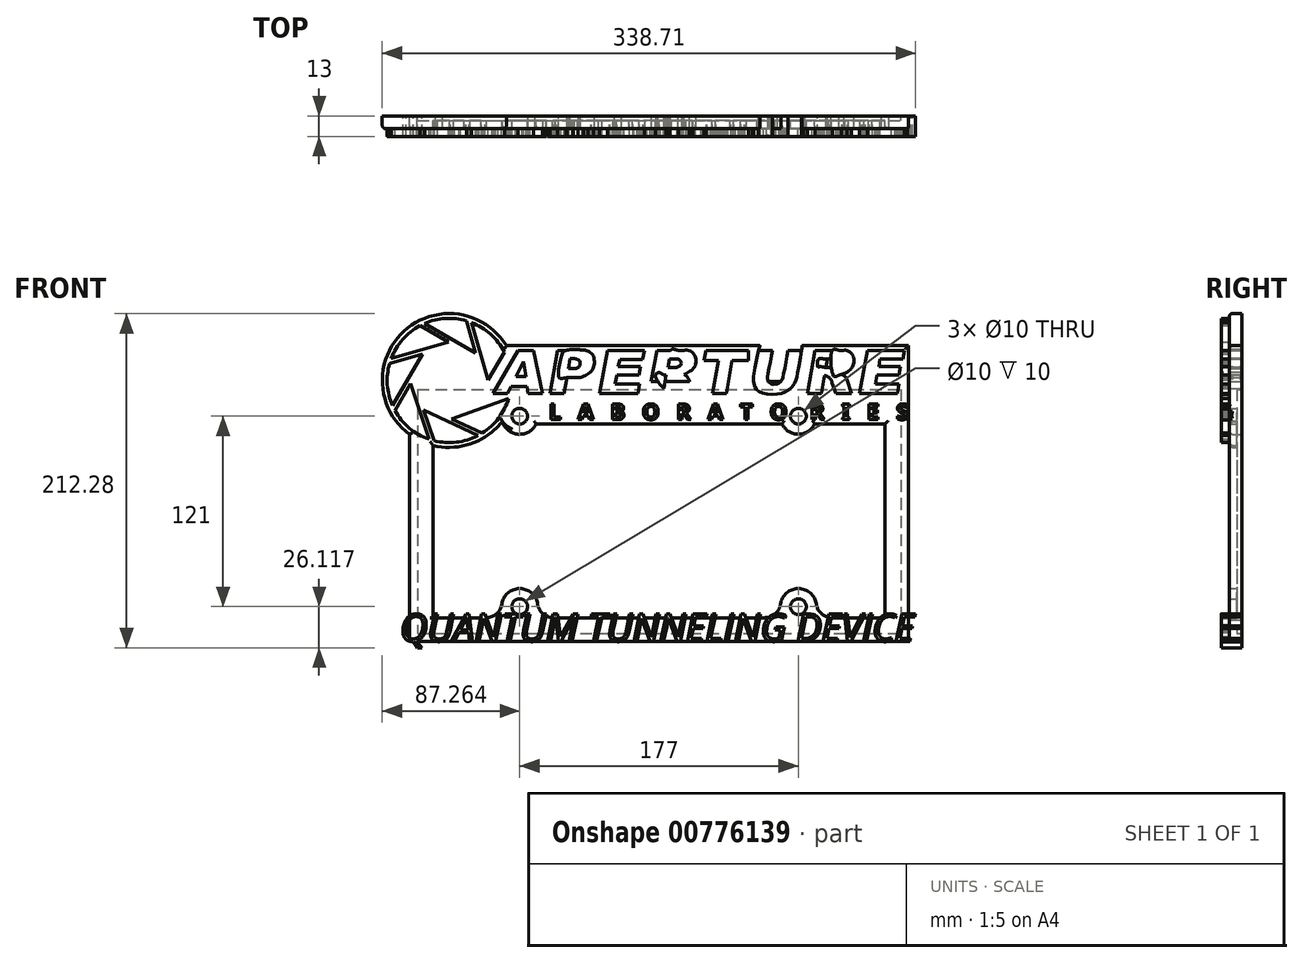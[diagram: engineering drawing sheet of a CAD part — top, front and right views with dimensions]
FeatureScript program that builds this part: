
annotation { "Feature Type Name" : "Feature", "Feature Type Description" : "" }
export const myFeature = defineFeature(function(context is Context, id is Id, definition is map)
    precondition{}
    {
        {
            var Q0;
            Q0=qCreatedBy(makeId("Front.planeOp"),FACE);
            var sketch = newSketch(context, id + "F0", { "sketchPlane" : qUnion([Q0])});
            skLineSegment(sketch, "E0.bottom", {"start": v(-247.83, 125.5) * mm, "end": v(59.17, 125.5) * mm});
            skLineSegment(sketch, "E0.top", {"start": v(-247.83, -29.5) * mm, "end": v(59.17, -29.5) * mm});
            skLineSegment(sketch, "E0.left", {"start": v(-247.83, 125.5) * mm, "end": v(-247.83, -29.5) * mm});
            skLineSegment(sketch, "E0.right", {"start": v(59.17, 125.5) * mm, "end": v(59.17, -29.5) * mm});
            skCircle(sketch, "E1", {"center": v(-182.83, 108.5) * mm, "radius": 5 * mm});
            skCircle(sketch, "E2", {"center": v(-5.83, 108.5) * mm, "radius": 5 * mm});
            skCircle(sketch, "E3", {"center": v(-182.83, -12.5) * mm, "radius": 5 * mm});
            skCircle(sketch, "E4", {"center": v(-5.83, -12.5) * mm, "radius": 5 * mm});
            skLineSegment(sketch, "E5.bottom", {"start": v(-252.83, 130.5) * mm, "end": v(64.17, 130.5) * mm});
            skLineSegment(sketch, "E5.top", {"start": v(-252.83, -34.5) * mm, "end": v(64.17, -34.5) * mm});
            skLineSegment(sketch, "E5.left", {"start": v(-252.83, 130.5) * mm, "end": v(-252.83, -34.5) * mm});
            skLineSegment(sketch, "E5.right", {"start": v(64.17, 130.5) * mm, "end": v(64.17, -34.5) * mm});
            skLineSegment(sketch, "E6.bottom", {"start": v(49.17, 115.5) * mm, "end": v(15.46, 115.5) * mm});
            skLineSegment(sketch, "E6.top", {"start": v(49.17, -19.5) * mm, "end": v(15.46, -19.5) * mm});
            skLineSegment(sketch, "E6.left", {"start": v(49.17, 115.5) * mm, "end": v(49.17, -19.5) * mm});
            skLineSegment(sketch, "E6.right", {"start": v(-237.83, 115.5) * mm, "end": v(-237.83, -19.5) * mm});
            skArc(sketch, "E7", {"start": v(-17.21, 106.9) * mm, "mid": v(-5.83, 97) * mm, "end": v(5.56, 106.9) * mm});
            skArc(sketch, "E8", {"start": v(-194.21, 106.9) * mm, "mid": v(-182.83, 97) * mm, "end": v(-171.44, 106.9) * mm});
            skArc(sketch, "E9", {"start": v(-171.44, -10.89) * mm, "mid": v(-182.83, -1) * mm, "end": v(-194.21, -10.89) * mm});
            skLineSegment(sketch, "E10.trimOffspring", {"start": v(-204.12, -19.5) * mm, "end": v(-237.83, -19.5) * mm});
            skLineSegment(sketch, "E11.trimOffspring", {"start": v(-204.12, 115.5) * mm, "end": v(-237.83, 115.5) * mm});
            skLineSegment(sketch, "E12.trimOffspring", {"start": v(-27.12, 115.5) * mm, "end": v(-161.54, 115.5) * mm});
            skArc(sketch, "E13", {"start": v(5.56, -10.89) * mm, "mid": v(-5.83, -1) * mm, "end": v(-17.21, -10.89) * mm});
            skLineSegment(sketch, "E14.trimOffspring", {"start": v(-27.12, -19.5) * mm, "end": v(-161.54, -19.5) * mm});
            skPoint(sketch, "E15.visualSharp", {"position": v(-173.7, -19.5) * mm});
            skArc(sketch, "E15.filletArc", {"start": v(-171.44, -10.89) * mm, "mid": v(-168.1, -17.04) * mm, "end": v(-161.54, -19.5) * mm});
            skPoint(sketch, "E16.visualSharp", {"position": v(-191.95, -19.5) * mm});
            skArc(sketch, "E16.filletArc", {"start": v(-204.12, -19.5) * mm, "mid": v(-197.56, -17.04) * mm, "end": v(-194.21, -10.89) * mm});
            skPoint(sketch, "E17.visualSharp", {"position": v(-14.95, -19.5) * mm});
            skArc(sketch, "E17.filletArc", {"start": v(-27.12, -19.5) * mm, "mid": v(-20.56, -17.04) * mm, "end": v(-17.21, -10.89) * mm});
            skPoint(sketch, "E18.visualSharp", {"position": v(3.3, -19.5) * mm});
            skArc(sketch, "E18.filletArc", {"start": v(5.56, -10.89) * mm, "mid": v(8.9, -17.04) * mm, "end": v(15.46, -19.5) * mm});
            skPoint(sketch, "E19.visualSharp", {"position": v(3.3, 115.5) * mm});
            skArc(sketch, "E19.filletArc", {"start": v(15.46, 115.5) * mm, "mid": v(8.9, 113.05) * mm, "end": v(5.56, 106.9) * mm});
            skPoint(sketch, "E20.visualSharp", {"position": v(-14.95, 115.5) * mm});
            skArc(sketch, "E20.filletArc", {"start": v(-17.21, 106.9) * mm, "mid": v(-20.56, 113.05) * mm, "end": v(-27.12, 115.5) * mm});
            skPoint(sketch, "E21.visualSharp", {"position": v(-173.7, 115.5) * mm});
            skArc(sketch, "E21.filletArc", {"start": v(-161.54, 115.5) * mm, "mid": v(-168.1, 113.05) * mm, "end": v(-171.44, 106.9) * mm});
            skPoint(sketch, "E22.visualSharp", {"position": v(-191.95, 115.5) * mm});
            skArc(sketch, "E22.filletArc", {"start": v(-194.21, 106.9) * mm, "mid": v(-197.56, 113.05) * mm, "end": v(-204.12, 115.5) * mm});
            skSolve(sketch);
        }
        {
            var Q0;
            Q0=qCreatedBy(makeId("Front.planeOp"),FACE);
            var sketch = newSketch(context, id + "F1", { "sketchPlane" : qUnion([Q0])});
            skArc(sketch, "E23", {"start": v(-237.3, 92.95) * mm, "mid": v(-223.07, 92) * mm, "end": v(-209.42, 96.17) * mm});
            skPoint(sketch, "E23.first.point", {"position": v(-258.83, 155.25) * mm});
            skPoint(sketch, "E23.second.point", {"position": v(-223.83, 91.92) * mm});
            skPoint(sketch, "E23.third.point", {"position": v(-267, 132.67) * mm});
            skLineSegment(sketch, "E24", {"start": v(-246.07, 166.01) * mm, "end": v(-228.04, 155.5) * mm});
            skLineSegment(sketch, "E25", {"start": v(-228.04, 155.5) * mm, "end": v(-264.5, 145.07) * mm});
            skLineSegment(sketch, "E26", {"start": v(-243.18, 167.4) * mm, "end": v(-210.8, 148.54) * mm});
            skLineSegment(sketch, "E27", {"start": v(-210.8, 148.54) * mm, "end": v(-216.68, 169.07) * mm});
            skLineSegment(sketch, "E28", {"start": v(-213.44, 167.98) * mm, "end": v(-203, 131.5) * mm});
            skLineSegment(sketch, "E29", {"start": v(-203, 131.5) * mm, "end": v(-192.6, 149.36) * mm});
            skLineSegment(sketch, "E30", {"start": v(-265.5, 142.08) * mm, "end": v(-244.59, 148.07) * mm});
            skLineSegment(sketch, "E31", {"start": v(-244.59, 148.07) * mm, "end": v(-263.68, 115.27) * mm});
            skLineSegment(sketch, "E32", {"start": v(-262.1, 112.08) * mm, "end": v(-252.17, 129.12) * mm});
            skLineSegment(sketch, "E33", {"start": v(-252.17, 129.12) * mm, "end": v(-240.5, 93.9) * mm});
            skLineSegment(sketch, "E34", {"start": v(-237.3, 92.95) * mm, "end": v(-243.8, 112.5) * mm});
            skLineSegment(sketch, "E35", {"start": v(-243.8, 112.5) * mm, "end": v(-209.42, 96.17) * mm});
            skLineSegment(sketch, "E36", {"start": v(-206.72, 97.71) * mm, "end": v(-226, 106.88) * mm});
            skLineSegment(sketch, "E37", {"start": v(-226, 106.88) * mm, "end": v(-189.8, 119.9) * mm});
            skArc(sketch, "E38.trimOffspring", {"start": v(-206.72, 97.71) * mm, "mid": v(-196.24, 107.26) * mm, "end": v(-189.8, 119.9) * mm});
            skArc(sketch, "E39.trimOffspring", {"start": v(-262.1, 112.08) * mm, "mid": v(-252.98, 101) * mm, "end": v(-240.5, 93.9) * mm});
            skArc(sketch, "E40.trimOffspring", {"start": v(-265.5, 142.08) * mm, "mid": v(-266.94, 128.52) * mm, "end": v(-263.68, 115.27) * mm});
            skArc(sketch, "E41.trimOffspring", {"start": v(-246.07, 166.01) * mm, "mid": v(-257.2, 157.22) * mm, "end": v(-264.5, 145.07) * mm});
            skArc(sketch, "E42.trimOffspring", {"start": v(-216.68, 169.07) * mm, "mid": v(-230.08, 170.53) * mm, "end": v(-243.18, 167.4) * mm});
            skArc(sketch, "E43.trimOffspring", {"start": v(-192.6, 149.36) * mm, "mid": v(-201.32, 160.58) * mm, "end": v(-213.44, 167.98) * mm});
            skArc(sketch, "E44", {"start": v(-191.32, 153.32) * mm, "mid": v(-269.71, 136.84) * mm, "end": v(-198.47, 100.23) * mm});
            skLineSegment(sketch, "E45", {"start": v(-191.32, 153.32) * mm, "end": v(64.17, 153.32) * mm});
            skLineSegment(sketch, "E46", {"start": v(64.17, 153.32) * mm, "end": v(64.17, 128.47) * mm});
            skLineSegment(sketch, "E47", {"start": v(-199.68, 123) * mm, "end": v(-183.75, 150.32) * mm});
            skLineSegment(sketch, "E48", {"start": v(-183.75, 150.32) * mm, "end": v(-174.2, 150.32) * mm});
            skLineSegment(sketch, "E49", {"start": v(-174.2, 150.32) * mm, "end": v(-168.23, 123) * mm});
            skLineSegment(sketch, "E50", {"start": v(-168.23, 123) * mm, "end": v(-177.57, 123) * mm});
            skLineSegment(sketch, "E51", {"start": v(-177.57, 123) * mm, "end": v(-178.26, 127.46) * mm});
            skLineSegment(sketch, "E52", {"start": v(-178.26, 127.46) * mm, "end": v(-188.28, 127.46) * mm});
            skLineSegment(sketch, "E53", {"start": v(-188.28, 127.46) * mm, "end": v(-190.41, 123) * mm});
            skLineSegment(sketch, "E54", {"start": v(-190.41, 123) * mm, "end": v(-199.68, 123) * mm});
            skLineSegment(sketch, "E55", {"start": v(-185.06, 133.84) * mm, "end": v(-180.46, 143.25) * mm});
            skLineSegment(sketch, "E56", {"start": v(-180.46, 143.25) * mm, "end": v(-178.88, 133.64) * mm});
            skLineSegment(sketch, "E57", {"start": v(-178.88, 133.64) * mm, "end": v(-185.06, 133.84) * mm});
            skLineSegment(sketch, "E58", {"start": v(-163.56, 123) * mm, "end": v(-158.67, 150.32) * mm});
            skLineSegment(sketch, "E59", {"start": v(-158.67, 150.32) * mm, "end": v(-140.86, 150.32) * mm});
            skLineSegment(sketch, "E60", {"start": v(-163.56, 123) * mm, "end": v(-154.65, 123) * mm});
            skLineSegment(sketch, "E61", {"start": v(-154.65, 123) * mm, "end": v(-152.8, 133.06) * mm});
            skLineSegment(sketch, "E62", {"start": v(-152.8, 133.06) * mm, "end": v(-145.58, 133.06) * mm});
            skLineSegment(sketch, "E63", {"start": v(-150.74, 145) * mm, "end": v(-151.94, 138.81) * mm});
            skPoint(sketch, "E64.12.internal.snap0", {"position": v(-151.34, 141.9) * mm});
            skFitSpline(sketch, "E64", {"points": [v(-150.74, 145) * mm, v(-147.48, 145) * mm, v(-145.9, 144.52) * mm, v(-144.71, 143.37) * mm, v(-144.5, 142.29) * mm, v(-144.66, 140.5) * mm, v(-145.9, 139.4) * mm, v(-147.8, 138.76) * mm, v(-151.94, 138.81) * mm, v(-153.46, 138.81) * mm, v(-155.03, 138.81) * mm, v(-155.2, 140.17) * mm, v(-154.65, 141.9) * mm, v(-153.9, 145) * mm, v(-152.75, 145) * mm, v(-150.74, 145) * mm]});
            skFitSpline(sketch, "E65", {"points": [v(-140.86, 150.32) * mm, v(-138.78, 149.57) * mm, v(-136.84, 148.03) * mm, v(-135.81, 146.08) * mm, v(-135.45, 143.16) * mm, v(-135.7, 140.7) * mm, v(-136.84, 137.77) * mm, v(-138.02, 136.39) * mm, v(-140.02, 134.85) * mm, v(-142.68, 133.67) * mm, v(-145.58, 133.06) * mm, v(-152.8, 133.06) * mm, v(-157.81, 133.06) * mm, v(-156.38, 146.6) * mm, v(-153.56, 150.32) * mm, v(-140.86, 150.32) * mm]});
            skLineSegment(sketch, "E66", {"start": v(-127.1, 150.38) * mm, "end": v(-103.53, 150.38) * mm});
            skLineSegment(sketch, "E67", {"start": v(-103.53, 150.38) * mm, "end": v(-104.72, 144.46) * mm});
            skLineSegment(sketch, "E68", {"start": v(-104.72, 144.46) * mm, "end": v(-119.26, 144.46) * mm});
            skLineSegment(sketch, "E69", {"start": v(-119.26, 144.46) * mm, "end": v(-120.24, 140.2) * mm});
            skLineSegment(sketch, "E70", {"start": v(-120.24, 140.2) * mm, "end": v(-106.23, 140.2) * mm});
            skLineSegment(sketch, "E71", {"start": v(-106.23, 140.2) * mm, "end": v(-107.21, 134.6) * mm});
            skLineSegment(sketch, "E72", {"start": v(-107.21, 134.6) * mm, "end": v(-121.12, 134.6) * mm});
            skLineSegment(sketch, "E73", {"start": v(-121.12, 134.6) * mm, "end": v(-122.21, 129.04) * mm});
            skLineSegment(sketch, "E74", {"start": v(-122.21, 129.04) * mm, "end": v(-106.85, 129.04) * mm});
            skLineSegment(sketch, "E75", {"start": v(-106.85, 129.04) * mm, "end": v(-107.84, 122.92) * mm});
            skLineSegment(sketch, "E76", {"start": v(-107.84, 122.92) * mm, "end": v(-132.23, 122.92) * mm});
            skLineSegment(sketch, "E77", {"start": v(-132.23, 122.92) * mm, "end": v(-127.1, 150.38) * mm});
            skLineSegment(sketch, "E78", {"start": v(-64.64, 150.38) * mm, "end": v(-37.58, 150.38) * mm});
            skLineSegment(sketch, "E79", {"start": v(-37.58, 150.38) * mm, "end": v(-37.58, 143.85) * mm});
            skLineSegment(sketch, "E80", {"start": v(-37.58, 143.85) * mm, "end": v(-47.88, 143.85) * mm});
            skLineSegment(sketch, "E81", {"start": v(-47.88, 143.85) * mm, "end": v(-51.56, 122.92) * mm});
            skLineSegment(sketch, "E82", {"start": v(-51.56, 122.92) * mm, "end": v(-60.33, 122.92) * mm});
            skLineSegment(sketch, "E83", {"start": v(-60.33, 122.92) * mm, "end": v(-56.65, 143.85) * mm});
            skLineSegment(sketch, "E84", {"start": v(-56.65, 143.85) * mm, "end": v(-65.71, 143.85) * mm});
            skLineSegment(sketch, "E85", {"start": v(-65.71, 143.85) * mm, "end": v(-64.64, 150.38) * mm});
            skLineSegment(sketch, "E86", {"start": v(38.19, 150.38) * mm, "end": v(61.68, 150.38) * mm});
            skLineSegment(sketch, "E87", {"start": v(61.68, 150.38) * mm, "end": v(60.69, 144.74) * mm});
            skLineSegment(sketch, "E88", {"start": v(60.69, 144.74) * mm, "end": v(46.1, 144.74) * mm});
            skLineSegment(sketch, "E89", {"start": v(46.1, 144.74) * mm, "end": v(45.31, 140.2) * mm});
            skLineSegment(sketch, "E90", {"start": v(45.31, 140.2) * mm, "end": v(59.09, 140.2) * mm});
            skLineSegment(sketch, "E91", {"start": v(59.09, 140.2) * mm, "end": v(58.1, 134.6) * mm});
            skLineSegment(sketch, "E92", {"start": v(58.1, 134.6) * mm, "end": v(44.13, 134.6) * mm});
            skLineSegment(sketch, "E93", {"start": v(44.13, 134.6) * mm, "end": v(43.15, 129.04) * mm});
            skLineSegment(sketch, "E94", {"start": v(43.15, 129.04) * mm, "end": v(58.1, 129.04) * mm});
            skLineSegment(sketch, "E95", {"start": v(58.1, 129.04) * mm, "end": v(57.02, 122.92) * mm});
            skLineSegment(sketch, "E96", {"start": v(57.02, 122.92) * mm, "end": v(33, 122.92) * mm});
            skLineSegment(sketch, "E97", {"start": v(33, 122.92) * mm, "end": v(38.19, 150.38) * mm});
            skLineSegment(sketch, "E98", {"start": v(-89.8, 134.6) * mm, "end": v(-91.85, 122.92) * mm});
            skLineSegment(sketch, "E99", {"start": v(-91.85, 122.92) * mm, "end": v(-100.78, 122.92) * mm});
            skLineSegment(sketch, "E100", {"start": v(-100.78, 122.92) * mm, "end": v(-95.52, 150.38) * mm});
            skLineSegment(sketch, "E101", {"start": v(-95.52, 150.38) * mm, "end": v(-78.58, 150.38) * mm});
            skLineSegment(sketch, "E102", {"start": v(-72.38, 122.92) * mm, "end": v(-82.38, 122.92) * mm});
            skLineSegment(sketch, "E103", {"start": v(-87.64, 144.93) * mm, "end": v(-88.6, 139.45) * mm});
            skLineSegment(sketch, "E104", {"start": v(-31.18, 150.38) * mm, "end": v(-22.4, 150.38) * mm});
            skLineSegment(sketch, "E105", {"start": v(-12.5, 150.38) * mm, "end": v(-3.78, 150.38) * mm});
            skLineSegment(sketch, "E106", {"start": v(27.9, 122.92) * mm, "end": v(18.18, 122.92) * mm});
            skLineSegment(sketch, "E107", {"start": v(10.75, 134.6) * mm, "end": v(8.7, 122.92) * mm});
            skLineSegment(sketch, "E108", {"start": v(8.7, 122.92) * mm, "end": v(0, 122.92) * mm});
            skLineSegment(sketch, "E109", {"start": v(0, 122.92) * mm, "end": v(4.83, 150.38) * mm});
            skLineSegment(sketch, "E110", {"start": v(4.83, 150.38) * mm, "end": v(23.13, 150.38) * mm});
            skLineSegment(sketch, "E111", {"start": v(12.73, 144.93) * mm, "end": v(11.77, 139.45) * mm});
            skFitSpline(sketch, "E112", {"points": [v(-78.58, 150.38) * mm, v(-76.22, 150.38) * mm, v(-73.84, 149.53) * mm, v(-72, 147.8) * mm, v(-71.08, 145.52) * mm, v(-70.92, 142.87) * mm, v(-71.25, 141.09) * mm, v(-72.38, 138.93) * mm, v(-73.79, 137.57) * mm, v(-76.11, 136.11) * mm, v(-78.58, 135.09) * mm, v(-83.9, 134.6) * mm, v(-88.22, 134.6) * mm, v(-87.05, 150.38) * mm, v(-82.38, 150.38) * mm, v(-78.58, 150.38) * mm]});
            skFitSpline(sketch, "E113", {"points": [v(-78.58, 135.09) * mm, v(-76.98, 134.06) * mm, v(-75.63, 132.22) * mm, v(-74.44, 129.25) * mm, v(-72.38, 122.92) * mm, v(-71.52, 120.49) * mm, v(-70.81, 118.6) * mm, v(-81.14, 127.3) * mm, v(-82, 136.82) * mm, v(-80.22, 136) * mm, v(-78.58, 135.09) * mm]});
            skFitSpline(sketch, "E114", {"points": [v(-89.8, 134.6) * mm, v(-87.36, 133.57) * mm, v(-85.47, 131.25) * mm, v(-85.03, 129.2) * mm, v(-83.95, 126.54) * mm, v(-82.38, 122.92) * mm, v(-80.44, 120.7) * mm, v(-80.65, 118.32) * mm, v(-96.55, 133.68) * mm, v(-94.12, 136.17) * mm, v(-91.1, 134.6) * mm, v(-89.8, 134.6) * mm]});
            skFitSpline(sketch, "E115", {"points": [v(-31.18, 150.38) * mm, v(-34.42, 131.99) * mm, v(-34.21, 129.96) * mm, v(-33.72, 127.64) * mm, v(-32.53, 125.61) * mm, v(-30.3, 123.86) * mm, v(-25.88, 122.46) * mm, v(-19.3, 122.53) * mm, v(-14.96, 123.51) * mm, v(-11.31, 125.82) * mm, v(-8.44, 129.11) * mm, v(-6.9, 132.34) * mm, v(-6.27, 135.98) * mm, v(-3.78, 150.38) * mm, v(-3.05, 155.51) * mm, v(-3.05, 158.8) * mm, v(-30.01, 159.37) * mm, v(-30.3, 156.21) * mm, v(-30.5, 152.36) * mm, v(-31.18, 150.38) * mm]});
            skFitSpline(sketch, "E116", {"points": [v(-22.4, 150.38) * mm, v(-25.29, 134.18) * mm, v(-25.29, 132.02) * mm, v(-24.9, 130.65) * mm, v(-23.92, 129.62) * mm, v(-22.4, 128.88) * mm, v(-20.5, 128.83) * mm, v(-18.74, 129.34) * mm, v(-17.2, 130.3) * mm, v(-16.23, 131.79) * mm, v(-15.6, 133.78) * mm, v(-12.5, 150.38) * mm, v(-11.67, 156.07) * mm, v(-11.27, 158.46) * mm, v(-21.07, 158.92) * mm, v(-21.36, 156.47) * mm, v(-21.87, 155.33) * mm, v(-22.4, 150.38) * mm]});
            skFitSpline(sketch, "E117", {"points": [v(12.73, 144.93) * mm, v(16.74, 144.93) * mm, v(18.3, 144.5) * mm, v(19.87, 143.6) * mm, v(20.28, 142.54) * mm, v(20.02, 141.38) * mm, v(18.86, 140.16) * mm, v(16.8, 139.46) * mm, v(13.71, 139.3) * mm, v(11.77, 139.45) * mm, v(7.65, 139.91) * mm, v(6.39, 139.96) * mm, v(7.1, 144.93) * mm, v(9.67, 144.93) * mm, v(12.73, 144.93) * mm]});
            skFitSpline(sketch, "E118", {"points": [v(23.13, 150.38) * mm, v(24.42, 150.38) * mm, v(26.39, 149.56) * mm, v(27.6, 148.6) * mm, v(28.81, 146.93) * mm, v(29.27, 145.67) * mm, v(29.47, 143.6) * mm, v(29.27, 141.63) * mm, v(28.2, 139.3) * mm, v(26.8, 137.74) * mm, v(25.07, 136.53) * mm, v(23.5, 135.72) * mm, v(21.39, 135.06) * mm, v(19.06, 134.15) * mm, v(16.64, 134) * mm, v(15.78, 150.38) * mm, v(19.82, 150.38) * mm, v(23.13, 150.38) * mm]});
            skArc(sketch, "E119", {"start": v(26.39, 149.56) * mm, "mid": v(24.81, 150.17) * mm, "end": v(23.13, 150.38) * mm});
            skArc(sketch, "E120", {"start": v(15.5, 129.45) * mm, "mid": v(14.07, 132.82) * mm, "end": v(10.69, 134.23) * mm});
            skArc(sketch, "E121", {"start": v(24.93, 131.86) * mm, "mid": v(23.55, 133.9) * mm, "end": v(21.39, 135.06) * mm});
            skLineSegment(sketch, "E122", {"start": v(15.5, 129.45) * mm, "end": v(18.18, 122.92) * mm});
            skLineSegment(sketch, "E123", {"start": v(24.93, 131.86) * mm, "end": v(27.9, 122.92) * mm});
            skText(sketch, "E124", { "text": " L   A   B   O   R   A   T   O    R   I   E   S", "fontName": "NotoSans-Bold.ttf"});
            skLineSegment(sketch, "E125", {"start": v(64.17, 103.55) * mm, "end": v(-171.66, 103.55) * mm});
            skLineSegment(sketch, "E126", {"start": v(64.17, 103.55) * mm, "end": v(64.17, 128.47) * mm});
            skFitSpline(sketch, "E127", {"points": [v(-87.64, 144.93) * mm, v(-83.83, 144.93) * mm, v(-81.83, 144.41) * mm, v(-80.56, 143.47) * mm, v(-80.2, 142.57) * mm, v(-80.4, 141.39) * mm, v(-81.1, 140.49) * mm, v(-82.08, 140) * mm, v(-84.12, 139.38) * mm, v(-85.5, 139.3) * mm, v(-88.6, 139.45) * mm, v(-90.9, 139.45) * mm, v(-92.46, 139.45) * mm, v(-91.93, 145.47) * mm, v(-90.58, 144.93) * mm, v(-88.98, 144.93) * mm, v(-87.64, 144.93) * mm]});
            skText(sketch, "E128", { "text": "QUANTUM TUNNELING DEVICE", "fontName": "OpenSans-Italic.ttf"});
            skLineSegment(sketch, "E129", {"start": v(-171.66, 103.55) * mm, "end": v(-177.35, 103.55) * mm});
            skArc(sketch, "E130", {"start": v(-191.23, 102.4) * mm, "mid": v(-184.13, 101.03) * mm, "end": v(-177.35, 103.55) * mm});
            skPoint(sketch, "E131.visualSharp", {"position": v(-193.14, 103.55) * mm});
            skArc(sketch, "E132", {"start": v(-198.47, 100.23) * mm, "mid": v(-196.08, 102.66) * mm, "end": v(-193.94, 105.3) * mm});
            skArc(sketch, "E133", {"start": v(-193.94, 105.3) * mm, "mid": v(-192.7, 103.75) * mm, "end": v(-191.23, 102.4) * mm});
            const initialGuessF1  = {"E124": [-0.16794, 0.10632, 1, 0, 0.01], "E128": [-0.25883, -0.0345, 1, 0, 0.01742]};
            skSetInitialGuess(sketch, initialGuessF1);
            skSolve(sketch);
        }
        {
            var Q0;
            Q0=makeQuery(id+"F1.imprint","IMPRINT",FACE,{"disambiguationData":[TD([[makeQuery(id+"F1.imprint","IMPRINT",EDGE,{"derivedFrom":sQuery(id+"F1.wireOp",EDGE,"E124.sketch_text.stroke-141")}),-1.0]])]});
            var Q1;
            Q1=makeQuery(id+"F1.imprint","IMPRINT",FACE,{"disambiguationData":[TD([[makeQuery(id+"F1.imprint","IMPRINT",EDGE,{"derivedFrom":sQuery(id+"F1.wireOp",EDGE,"E47")}),-1.0]])]});
            var Q2;
            Q2=makeQuery(id+"F0.imprint","IMPRINT",FACE,{"disambiguationData":[TD([[makeQuery(id+"F0.imprint","IMPRINT",EDGE,{"derivedFrom":sQuery(id+"F0.wireOp",EDGE,"E0.bottom")}),1.0]])]});
            var Q3;
            Q3=makeQuery(id+"F0.imprint","IMPRINT",FACE,{"disambiguationData":[TD([[makeQuery(id+"F0.imprint","IMPRINT",EDGE,{"derivedFrom":sQuery(id+"F0.wireOp",EDGE,"E1")}),1.0]])]});
            var Q4;
            Q4=makeQuery(id+"F0.imprint","IMPRINT",FACE,{"disambiguationData":[TD([[makeQuery(id+"F0.imprint","IMPRINT",EDGE,{"derivedFrom":sQuery(id+"F0.wireOp",EDGE,"E2")}),1.0]])]});
            var Q5;
            Q5=makeQuery(id+"F0.imprint","IMPRINT",FACE,{"disambiguationData":[TD([[makeQuery(id+"F0.imprint","IMPRINT",EDGE,{"derivedFrom":sQuery(id+"F0.wireOp",EDGE,"E3")}),1.0]])]});
            var Q6;
            Q6=makeQuery(id+"F0.imprint","IMPRINT",FACE,{"disambiguationData":[TD([[makeQuery(id+"F0.imprint","IMPRINT",EDGE,{"derivedFrom":sQuery(id+"F0.wireOp",EDGE,"E4")}),1.0]])]});
            var Q7;
            Q7=makeQuery(id+"F0.imprint","IMPRINT",FACE,{"disambiguationData":[TD([[makeQuery(id+"F0.imprint","IMPRINT",EDGE,{"derivedFrom":sQuery(id+"F0.wireOp",EDGE,"E0.bottom")}),-1.0]])]});
            var Q8;
            Q8=makeQuery(id+"F1.imprint","IMPRINT",FACE,{"disambiguationData":[TD([[makeQuery(id+"F1.imprint","IMPRINT",EDGE,{"derivedFrom":sQuery(id+"F1.wireOp",EDGE,"E28")}),1.0]])]});
            var Q9;
            Q9=makeQuery(id+"F1.imprint","IMPRINT",FACE,{"disambiguationData":[TD([[makeQuery(id+"F1.imprint","IMPRINT",EDGE,{"derivedFrom":sQuery(id+"F1.wireOp",EDGE,"E124.sketch_text.stroke-51")}),1.0]])]});
            var Q10;
            Q10=makeQuery(id+"F1.imprint","IMPRINT",FACE,{"disambiguationData":[TD([[makeQuery(id+"F1.imprint","IMPRINT",EDGE,{"derivedFrom":sQuery(id+"F1.wireOp",EDGE,"E23")}),1.0]])]});
            var Q11;
            Q11=makeQuery(id+"F1.imprint","IMPRINT",FACE,{"disambiguationData":[TD([[makeQuery(id+"F1.imprint","IMPRINT",EDGE,{"derivedFrom":sQuery(id+"F1.wireOp",EDGE,"E24")}),-1.0]])]});
            var Q12;
            Q12=makeQuery(id+"F1.imprint","IMPRINT",FACE,{"disambiguationData":[TD([[makeQuery(id+"F1.imprint","IMPRINT",EDGE,{"derivedFrom":sQuery(id+"F1.wireOp",EDGE,"E30")}),-1.0]])]});
            var Q13;
            Q13=makeQuery(id+"F1.imprint","IMPRINT",FACE,{"disambiguationData":[TD([[makeQuery(id+"F1.imprint","IMPRINT",EDGE,{"derivedFrom":sQuery(id+"F1.wireOp",EDGE,"E104")}),-1.0]])]});
            var Q14;
            Q14=makeQuery(id+"F1.imprint","IMPRINT",FACE,{"disambiguationData":[TD([[makeQuery(id+"F1.imprint","IMPRINT",EDGE,{"derivedFrom":sQuery(id+"F1.wireOp",EDGE,"E26")}),1.0]])]});
            var Q15;
            Q15=makeQuery(id+"F1.imprint","IMPRINT",FACE,{"disambiguationData":[TD([[makeQuery(id+"F1.imprint","IMPRINT",EDGE,{"derivedFrom":sQuery(id+"F1.wireOp",EDGE,"E32")}),-1.0]])]});
            var Q16;
            Q16=makeQuery(id+"F1.imprint","IMPRINT",FACE,{"disambiguationData":[TD([[makeQuery(id+"F1.imprint","IMPRINT",EDGE,{"derivedFrom":sQuery(id+"F1.wireOp",EDGE,"E36")}),-1.0]])]});
            var Q17;
            Q17=makeQuery(id+"F1.imprint","IMPRINT",FACE,{"disambiguationData":[TD([[makeQuery(id+"F1.imprint","IMPRINT",EDGE,{"derivedFrom":sQuery(id+"F1.wireOp",EDGE,"E66")}),-1.0]])]});
            var Q18;
            Q18=makeQuery(id+"F1.imprint","IMPRINT",FACE,{"disambiguationData":[TD([[makeQuery(id+"F1.imprint","IMPRINT",EDGE,{"derivedFrom":sQuery(id+"F1.wireOp",EDGE,"E78")}),-1.0]])]});
            var Q19;
            Q19=makeQuery(id+"F1.imprint","IMPRINT",FACE,{"disambiguationData":[TD([[makeQuery(id+"F1.imprint","IMPRINT",EDGE,{"derivedFrom":sQuery(id+"F1.wireOp",EDGE,"E86")}),-1.0]])]});
            var Q20;
            Q20=makeQuery(id+"F1.imprint","IMPRINT",FACE,{"disambiguationData":[TD([[makeQuery(id+"F1.imprint","IMPRINT",EDGE,{"derivedFrom":sQuery(id+"F1.wireOp",EDGE,"E98")}),-1.0]])]});
            var Q21;
            Q21=makeQuery(id+"F1.imprint","IMPRINT",FACE,{"disambiguationData":[TD([[makeQuery(id+"F1.imprint","IMPRINT",EDGE,{"derivedFrom":sQuery(id+"F1.wireOp",EDGE,"E106")}),-1.0]])]});
            var Q22;
            Q22=makeQuery(id+"F1.imprint","IMPRINT",FACE,{"disambiguationData":[TD([[makeQuery(id+"F1.imprint","IMPRINT",EDGE,{"derivedFrom":sQuery(id+"F1.wireOp",EDGE,"E58")}),-1.0]])]});
            var Q23;
            Q23=makeQuery(id+"F1.imprint","IMPRINT",FACE,{"disambiguationData":[TD([[makeQuery(id+"F1.imprint","IMPRINT",EDGE,{"derivedFrom":sQuery(id+"F1.wireOp",EDGE,"E124.sketch_text.stroke-104")}),1.0]])]});
            var Q24;
            Q24=makeQuery(id+"F1.imprint","IMPRINT",FACE,{"disambiguationData":[TD([[makeQuery(id+"F1.imprint","IMPRINT",EDGE,{"derivedFrom":sQuery(id+"F1.wireOp",EDGE,"E124.sketch_text.stroke-129")}),-1.0]])]});
            var Q25;
            Q25=makeQuery(id+"F1.imprint","IMPRINT",FACE,{"disambiguationData":[TD([[makeQuery(id+"F1.imprint","IMPRINT",EDGE,{"derivedFrom":sQuery(id+"F1.wireOp",EDGE,"E124.sketch_text.stroke-153")}),-1.0]])]});
            var Q26;
            Q26=makeQuery(id+"F1.imprint","IMPRINT",FACE,{"disambiguationData":[TD([[makeQuery(id+"F1.imprint","IMPRINT",EDGE,{"derivedFrom":sQuery(id+"F1.wireOp",EDGE,"E124.sketch_text.stroke-76")}),-1.0]])]});
            var Q27;
            Q27=makeQuery(id+"F1.imprint","IMPRINT",FACE,{"disambiguationData":[TD([[makeQuery(id+"F1.imprint","IMPRINT",EDGE,{"derivedFrom":sQuery(id+"F1.wireOp",EDGE,"E124.sketch_text.stroke-37")}),1.0]])]});
            var Q28;
            Q28=makeQuery(id+"F1.imprint","IMPRINT",FACE,{"disambiguationData":[TD([[makeQuery(id+"F1.imprint","IMPRINT",EDGE,{"derivedFrom":sQuery(id+"F1.wireOp",EDGE,"E124.sketch_text.stroke-96")}),-1.0]])]});
            var Q29;
            Q29=makeQuery(id+"F1.imprint","IMPRINT",FACE,{"disambiguationData":[TD([[makeQuery(id+"F1.imprint","IMPRINT",EDGE,{"derivedFrom":sQuery(id+"F1.wireOp",EDGE,"E124.sketch_text.stroke-0")}),-1.0]])]});
            var Q30;
            Q30=makeQuery(id+"F1.imprint","IMPRINT",FACE,{"disambiguationData":[TD([[makeQuery(id+"F1.imprint","IMPRINT",EDGE,{"derivedFrom":sQuery(id+"F1.wireOp",EDGE,"E124.sketch_text.stroke-57")}),-1.0]])]});
            var Q31;
            Q31=makeQuery(id+"F1.imprint","IMPRINT",FACE,{"disambiguationData":[TD([[makeQuery(id+"F1.imprint","IMPRINT",EDGE,{"derivedFrom":sQuery(id+"F1.wireOp",EDGE,"E55")}),-1.0]])]});
            var Q32;
            Q32=makeQuery(id+"F1.imprint","IMPRINT",FACE,{"disambiguationData":[TD([[makeQuery(id+"F1.imprint","IMPRINT",EDGE,{"derivedFrom":sQuery(id+"F1.wireOp",EDGE,"E124.sketch_text.stroke-6")}),-1.0]])]});
            var Q33;
            Q33=makeQuery(id+"F1.imprint","IMPRINT",FACE,{"disambiguationData":[TD([[makeQuery(id+"F1.imprint","IMPRINT",EDGE,{"derivedFrom":sQuery(id+"F1.wireOp",EDGE,"E124.sketch_text.stroke-43")}),-1.0]])]});
            var Q34;
            Q34=makeQuery(id+"F1.imprint","IMPRINT",FACE,{"disambiguationData":[TD([[makeQuery(id+"F1.imprint","IMPRINT",EDGE,{"derivedFrom":sQuery(id+"F1.wireOp",EDGE,"E124.sketch_text.stroke-18")}),-1.0]])]});
            var Q35;
            Q35=makeQuery(id+"F1.imprint","IMPRINT",FACE,{"disambiguationData":[TD([[makeQuery(id+"F1.imprint","IMPRINT",EDGE,{"derivedFrom":sQuery(id+"F1.wireOp",EDGE,"E124.sketch_text.stroke-14")}),1.0]])]});
            var Q36;
            Q36=makeQuery(id+"F1.imprint","IMPRINT",FACE,{"disambiguationData":[TD([[makeQuery(id+"F1.imprint","IMPRINT",EDGE,{"derivedFrom":sQuery(id+"F1.wireOp",EDGE,"E124.sketch_text.stroke-88")}),-1.0]])]});
            var Q37;
            Q37=makeQuery(id+"F1.imprint","IMPRINT",FACE,{"disambiguationData":[TD([[makeQuery(id+"F1.imprint","IMPRINT",EDGE,{"derivedFrom":sQuery(id+"F1.wireOp",EDGE,"E124.sketch_text.stroke-57")}),1.0]])]});
            var Q38;
            Q38=makeQuery(id+"F1.imprint","IMPRINT",FACE,{"disambiguationData":[TD([[makeQuery(id+"F1.imprint","IMPRINT",EDGE,{"derivedFrom":sQuery(id+"F1.wireOp",EDGE,"E124.sketch_text.stroke-30")}),1.0]])]});
            var Q39;
            Q39=makeQuery(id+"F1.imprint","IMPRINT",FACE,{"disambiguationData":[TD([[makeQuery(id+"F1.imprint","IMPRINT",EDGE,{"derivedFrom":sQuery(id+"F1.wireOp",EDGE,"E124.sketch_text.stroke-110")}),-1.0]])]});
            var Q40;
            Q40=makeQuery(id+"F1.imprint","IMPRINT",FACE,{"disambiguationData":[TD([[makeQuery(id+"F1.imprint","IMPRINT",EDGE,{"derivedFrom":sQuery(id+"F1.wireOp",EDGE,"E124.sketch_text.stroke-84")}),1.0]])]});
            var Q41;
            Q41=makeQuery(id+"F1.imprint","IMPRINT",FACE,{"disambiguationData":[TD([[makeQuery(id+"F1.imprint","IMPRINT",EDGE,{"derivedFrom":sQuery(id+"F1.wireOp",EDGE,"E124.sketch_text.stroke-110")}),1.0]])]});
            var Q42;
            {var subQ0=sQuery(id+"F1.wireOp",EDGE,"E65");var subQ1=sQuery(id+"F1.wireOp",EDGE,"E62");var subQ2=makeQuery(id+"F1.imprint","INTERSECT",VERTEX,{"disambiguationData":[OD(0.0)],"derivedFrom":[subQ1,subQ0]});Q42=makeQuery(id+"F1.imprint","IMPRINT",FACE,{"disambiguationData":[TD([[makeQuery(id+"F1.imprint","IMPRINT",EDGE,{"disambiguationData":[TD([[subQ2,1.0]])],"derivedFrom":subQ1}),-1.0]])]});}
            var Q43;
            Q43=makeQuery(id+"F1.imprint","IMPRINT",FACE,{"disambiguationData":[TD([[makeQuery(id+"F1.imprint","IMPRINT",EDGE,{"derivedFrom":sQuery(id+"F1.wireOp",EDGE,"E23")}),-1.0]])]});
            var Q44;
            Q44=makeQuery(id+"F1.imprint","IMPRINT",FACE,{"disambiguationData":[TD([[makeQuery(id+"F1.imprint","IMPRINT",EDGE,{"derivedFrom":sQuery(id+"F1.wireOp",EDGE,"E111")}),1.0]])]});
            var Q45;
            Q45=makeQuery(id+"F1.imprint","IMPRINT",FACE,{"disambiguationData":[TD([[makeQuery(id+"F1.imprint","IMPRINT",EDGE,{"derivedFrom":sQuery(id+"F1.wireOp",EDGE,"E103")}),1.0]])]});
            var Q46;
            Q46=makeQuery(id+"F1.imprint","IMPRINT",FACE,{"disambiguationData":[TD([[makeQuery(id+"F1.imprint","IMPRINT",EDGE,{"derivedFrom":sQuery(id+"F1.wireOp",EDGE,"E63")}),1.0]])]});
            extrude(context, id + "F2", {"entities" : qUnion([Q0, Q1, Q2, Q3, Q4, Q5, Q6, Q7, Q8, Q9, Q10, Q11, Q12, Q13, Q14, Q15, Q16, Q17, Q18, Q19, Q20, Q21, Q22, Q23, Q24, Q25, Q26, Q27, Q28, Q29, Q30, Q31, Q32, Q33, Q34, Q35, Q36, Q37, Q38, Q39, Q40, Q41, Q42, Q43, Q44, Q45, Q46]), "depth" : 8 * mm, "offsetDistance" : 25 * mm});
        }
        {
            var Q0;
            Q0=makeQuery(id+"F1.imprint","IMPRINT",FACE,{"disambiguationData":[TD([[makeQuery(id+"F1.imprint","IMPRINT",EDGE,{"derivedFrom":sQuery(id+"F1.wireOp",EDGE,"E28")}),1.0]])]});
            var Q1;
            Q1=makeQuery(id+"F1.imprint","IMPRINT",FACE,{"disambiguationData":[TD([[makeQuery(id+"F1.imprint","IMPRINT",EDGE,{"derivedFrom":sQuery(id+"F1.wireOp",EDGE,"E26")}),1.0]])]});
            var Q2;
            Q2=makeQuery(id+"F1.imprint","IMPRINT",FACE,{"disambiguationData":[TD([[makeQuery(id+"F1.imprint","IMPRINT",EDGE,{"derivedFrom":sQuery(id+"F1.wireOp",EDGE,"E24")}),-1.0]])]});
            var Q3;
            Q3=makeQuery(id+"F1.imprint","IMPRINT",FACE,{"disambiguationData":[TD([[makeQuery(id+"F1.imprint","IMPRINT",EDGE,{"derivedFrom":sQuery(id+"F1.wireOp",EDGE,"E30")}),-1.0]])]});
            var Q4;
            Q4=makeQuery(id+"F1.imprint","IMPRINT",FACE,{"disambiguationData":[TD([[makeQuery(id+"F1.imprint","IMPRINT",EDGE,{"derivedFrom":sQuery(id+"F1.wireOp",EDGE,"E32")}),-1.0]])]});
            var Q5;
            Q5=makeQuery(id+"F1.imprint","IMPRINT",FACE,{"disambiguationData":[TD([[makeQuery(id+"F1.imprint","IMPRINT",EDGE,{"derivedFrom":sQuery(id+"F1.wireOp",EDGE,"E23")}),1.0]])]});
            var Q6;
            Q6=makeQuery(id+"F1.imprint","IMPRINT",FACE,{"disambiguationData":[TD([[makeQuery(id+"F1.imprint","IMPRINT",EDGE,{"derivedFrom":sQuery(id+"F1.wireOp",EDGE,"E36")}),-1.0]])]});
            var Q7;
            Q7=makeQuery(id+"F1.imprint","IMPRINT",FACE,{"disambiguationData":[TD([[makeQuery(id+"F1.imprint","IMPRINT",EDGE,{"derivedFrom":sQuery(id+"F1.wireOp",EDGE,"E47")}),-1.0]])]});
            var Q8;
            Q8=makeQuery(id+"F1.imprint","IMPRINT",FACE,{"disambiguationData":[TD([[makeQuery(id+"F1.imprint","IMPRINT",EDGE,{"derivedFrom":sQuery(id+"F1.wireOp",EDGE,"E58")}),-1.0]])]});
            var Q9;
            Q9=makeQuery(id+"F1.imprint","IMPRINT",FACE,{"disambiguationData":[TD([[makeQuery(id+"F1.imprint","IMPRINT",EDGE,{"derivedFrom":sQuery(id+"F1.wireOp",EDGE,"E66")}),-1.0]])]});
            var Q10;
            Q10=makeQuery(id+"F1.imprint","IMPRINT",FACE,{"disambiguationData":[TD([[makeQuery(id+"F1.imprint","IMPRINT",EDGE,{"derivedFrom":sQuery(id+"F1.wireOp",EDGE,"E78")}),-1.0]])]});
            var Q11;
            Q11=makeQuery(id+"F1.imprint","IMPRINT",FACE,{"disambiguationData":[TD([[makeQuery(id+"F1.imprint","IMPRINT",EDGE,{"derivedFrom":sQuery(id+"F1.wireOp",EDGE,"E104")}),-1.0]])]});
            var Q12;
            Q12=makeQuery(id+"F1.imprint","IMPRINT",FACE,{"disambiguationData":[TD([[makeQuery(id+"F1.imprint","IMPRINT",EDGE,{"derivedFrom":sQuery(id+"F1.wireOp",EDGE,"E106")}),-1.0]])]});
            var Q13;
            Q13=makeQuery(id+"F1.imprint","IMPRINT",FACE,{"disambiguationData":[TD([[makeQuery(id+"F1.imprint","IMPRINT",EDGE,{"derivedFrom":sQuery(id+"F1.wireOp",EDGE,"E86")}),-1.0]])]});
            var Q14;
            Q14=makeQuery(id+"F1.imprint","IMPRINT",FACE,{"disambiguationData":[TD([[makeQuery(id+"F1.imprint","IMPRINT",EDGE,{"derivedFrom":sQuery(id+"F1.wireOp",EDGE,"E124.sketch_text.stroke-153")}),-1.0]])]});
            var Q15;
            Q15=makeQuery(id+"F1.imprint","IMPRINT",FACE,{"disambiguationData":[TD([[makeQuery(id+"F1.imprint","IMPRINT",EDGE,{"derivedFrom":sQuery(id+"F1.wireOp",EDGE,"E124.sketch_text.stroke-141")}),-1.0]])]});
            var Q16;
            Q16=makeQuery(id+"F1.imprint","IMPRINT",FACE,{"disambiguationData":[TD([[makeQuery(id+"F1.imprint","IMPRINT",EDGE,{"derivedFrom":sQuery(id+"F1.wireOp",EDGE,"E124.sketch_text.stroke-129")}),-1.0]])]});
            var Q17;
            Q17=makeQuery(id+"F1.imprint","IMPRINT",FACE,{"disambiguationData":[TD([[makeQuery(id+"F1.imprint","IMPRINT",EDGE,{"derivedFrom":sQuery(id+"F1.wireOp",EDGE,"E124.sketch_text.stroke-110")}),-1.0]])]});
            var Q18;
            Q18=makeQuery(id+"F1.imprint","IMPRINT",FACE,{"disambiguationData":[TD([[makeQuery(id+"F1.imprint","IMPRINT",EDGE,{"derivedFrom":sQuery(id+"F1.wireOp",EDGE,"E124.sketch_text.stroke-96")}),-1.0]])]});
            var Q19;
            Q19=makeQuery(id+"F1.imprint","IMPRINT",FACE,{"disambiguationData":[TD([[makeQuery(id+"F1.imprint","IMPRINT",EDGE,{"derivedFrom":sQuery(id+"F1.wireOp",EDGE,"E124.sketch_text.stroke-88")}),-1.0]])]});
            var Q20;
            Q20=makeQuery(id+"F1.imprint","IMPRINT",FACE,{"disambiguationData":[TD([[makeQuery(id+"F1.imprint","IMPRINT",EDGE,{"derivedFrom":sQuery(id+"F1.wireOp",EDGE,"E124.sketch_text.stroke-76")}),-1.0]])]});
            var Q21;
            Q21=makeQuery(id+"F1.imprint","IMPRINT",FACE,{"disambiguationData":[TD([[makeQuery(id+"F1.imprint","IMPRINT",EDGE,{"derivedFrom":sQuery(id+"F1.wireOp",EDGE,"E124.sketch_text.stroke-57")}),-1.0]])]});
            var Q22;
            Q22=makeQuery(id+"F1.imprint","IMPRINT",FACE,{"disambiguationData":[TD([[makeQuery(id+"F1.imprint","IMPRINT",EDGE,{"derivedFrom":sQuery(id+"F1.wireOp",EDGE,"E124.sketch_text.stroke-43")}),-1.0]])]});
            var Q23;
            Q23=makeQuery(id+"F1.imprint","IMPRINT",FACE,{"disambiguationData":[TD([[makeQuery(id+"F1.imprint","IMPRINT",EDGE,{"derivedFrom":sQuery(id+"F1.wireOp",EDGE,"E124.sketch_text.stroke-18")}),-1.0]])]});
            var Q24;
            Q24=makeQuery(id+"F1.imprint","IMPRINT",FACE,{"disambiguationData":[TD([[makeQuery(id+"F1.imprint","IMPRINT",EDGE,{"derivedFrom":sQuery(id+"F1.wireOp",EDGE,"E124.sketch_text.stroke-6")}),-1.0]])]});
            var Q25;
            Q25=makeQuery(id+"F1.imprint","IMPRINT",FACE,{"disambiguationData":[TD([[makeQuery(id+"F1.imprint","IMPRINT",EDGE,{"derivedFrom":sQuery(id+"F1.wireOp",EDGE,"E124.sketch_text.stroke-0")}),-1.0]])]});
            var Q26;
            Q26=makeQuery(id+"F1.imprint","IMPRINT",FACE,{"disambiguationData":[TD([[makeQuery(id+"F1.imprint","IMPRINT",EDGE,{"derivedFrom":sQuery(id+"F1.wireOp",EDGE,"E98")}),-1.0]])]});
            extrude(context, id + "F3", {"entities" : qUnion([Q0, Q1, Q2, Q3, Q4, Q5, Q6, Q7, Q8, Q9, Q10, Q11, Q12, Q13, Q14, Q15, Q16, Q17, Q18, Q19, Q20, Q21, Q22, Q23, Q24, Q25, Q26]), "depth" : 13 * mm, "offsetDistance" : 25 * mm});
        }
        {
            var Q0;
            Q0=makeQuery(id+"F1.imprint","IMPRINT",FACE,{"disambiguationData":[TD([[makeQuery(id+"F1.imprint","IMPRINT",EDGE,{"derivedFrom":sQuery(id+"F1.wireOp",EDGE,"E128.sketch_text.stroke-0")}),-1.0]])]});
            var Q1;
            Q1=makeQuery(id+"F1.imprint","IMPRINT",FACE,{"disambiguationData":[TD([[makeQuery(id+"F1.imprint","IMPRINT",EDGE,{"derivedFrom":sQuery(id+"F1.wireOp",EDGE,"E128.sketch_text.stroke-24")}),-1.0]])]});
            var Q2;
            Q2=makeQuery(id+"F1.imprint","IMPRINT",FACE,{"disambiguationData":[TD([[makeQuery(id+"F1.imprint","IMPRINT",EDGE,{"derivedFrom":sQuery(id+"F1.wireOp",EDGE,"E128.sketch_text.stroke-40")}),-1.0]])]});
            var Q3;
            Q3=makeQuery(id+"F1.imprint","IMPRINT",FACE,{"disambiguationData":[TD([[makeQuery(id+"F1.imprint","IMPRINT",EDGE,{"derivedFrom":sQuery(id+"F1.wireOp",EDGE,"E128.sketch_text.stroke-53")}),-1.0]])]});
            var Q4;
            Q4=makeQuery(id+"F1.imprint","IMPRINT",FACE,{"disambiguationData":[TD([[makeQuery(id+"F1.imprint","IMPRINT",EDGE,{"derivedFrom":sQuery(id+"F1.wireOp",EDGE,"E128.sketch_text.stroke-67")}),-1.0]])]});
            var Q5;
            Q5=makeQuery(id+"F1.imprint","IMPRINT",FACE,{"disambiguationData":[TD([[makeQuery(id+"F1.imprint","IMPRINT",EDGE,{"derivedFrom":sQuery(id+"F1.wireOp",EDGE,"E128.sketch_text.stroke-75")}),-1.0]])]});
            var Q6;
            Q6=makeQuery(id+"F1.imprint","IMPRINT",FACE,{"disambiguationData":[TD([[makeQuery(id+"F1.imprint","IMPRINT",EDGE,{"derivedFrom":sQuery(id+"F1.wireOp",EDGE,"E128.sketch_text.stroke-91")}),-1.0]])]});
            var Q7;
            Q7=makeQuery(id+"F1.imprint","IMPRINT",FACE,{"disambiguationData":[TD([[makeQuery(id+"F1.imprint","IMPRINT",EDGE,{"derivedFrom":sQuery(id+"F1.wireOp",EDGE,"E128.sketch_text.stroke-110")}),-1.0]])]});
            var Q8;
            Q8=makeQuery(id+"F1.imprint","IMPRINT",FACE,{"disambiguationData":[TD([[makeQuery(id+"F1.imprint","IMPRINT",EDGE,{"derivedFrom":sQuery(id+"F1.wireOp",EDGE,"E128.sketch_text.stroke-118")}),-1.0]])]});
            var Q9;
            Q9=makeQuery(id+"F1.imprint","IMPRINT",FACE,{"disambiguationData":[TD([[makeQuery(id+"F1.imprint","IMPRINT",EDGE,{"derivedFrom":sQuery(id+"F1.wireOp",EDGE,"E128.sketch_text.stroke-134")}),-1.0]])]});
            var Q10;
            Q10=makeQuery(id+"F1.imprint","IMPRINT",FACE,{"disambiguationData":[TD([[makeQuery(id+"F1.imprint","IMPRINT",EDGE,{"derivedFrom":sQuery(id+"F1.wireOp",EDGE,"E128.sketch_text.stroke-148")}),-1.0]])]});
            var Q11;
            Q11=makeQuery(id+"F1.imprint","IMPRINT",FACE,{"disambiguationData":[TD([[makeQuery(id+"F1.imprint","IMPRINT",EDGE,{"derivedFrom":sQuery(id+"F1.wireOp",EDGE,"E128.sketch_text.stroke-162")}),-1.0]])]});
            var Q12;
            Q12=makeQuery(id+"F1.imprint","IMPRINT",FACE,{"disambiguationData":[TD([[makeQuery(id+"F1.imprint","IMPRINT",EDGE,{"derivedFrom":sQuery(id+"F1.wireOp",EDGE,"E128.sketch_text.stroke-174")}),-1.0]])]});
            var Q13;
            Q13=makeQuery(id+"F1.imprint","IMPRINT",FACE,{"disambiguationData":[TD([[makeQuery(id+"F1.imprint","IMPRINT",EDGE,{"derivedFrom":sQuery(id+"F1.wireOp",EDGE,"E128.sketch_text.stroke-180")}),-1.0]])]});
            var Q14;
            Q14=makeQuery(id+"F1.imprint","IMPRINT",FACE,{"disambiguationData":[TD([[makeQuery(id+"F1.imprint","IMPRINT",EDGE,{"derivedFrom":sQuery(id+"F1.wireOp",EDGE,"E128.sketch_text.stroke-184")}),-1.0]])]});
            var Q15;
            Q15=makeQuery(id+"F1.imprint","IMPRINT",FACE,{"disambiguationData":[TD([[makeQuery(id+"F1.imprint","IMPRINT",EDGE,{"derivedFrom":sQuery(id+"F1.wireOp",EDGE,"E128.sketch_text.stroke-198")}),-1.0]])]});
            var Q16;
            Q16=makeQuery(id+"F1.imprint","IMPRINT",FACE,{"disambiguationData":[TD([[makeQuery(id+"F1.imprint","IMPRINT",EDGE,{"derivedFrom":sQuery(id+"F1.wireOp",EDGE,"E128.sketch_text.stroke-279")}),-1.0]])]});
            var Q17;
            Q17=makeQuery(id+"F1.imprint","IMPRINT",FACE,{"disambiguationData":[TD([[makeQuery(id+"F1.imprint","IMPRINT",EDGE,{"derivedFrom":sQuery(id+"F1.wireOp",EDGE,"E128.sketch_text.stroke-262")}),-1.0]])]});
            var Q18;
            Q18=makeQuery(id+"F1.imprint","IMPRINT",FACE,{"disambiguationData":[TD([[makeQuery(id+"F1.imprint","IMPRINT",EDGE,{"derivedFrom":sQuery(id+"F1.wireOp",EDGE,"E128.sketch_text.stroke-258")}),-1.0]])]});
            var Q19;
            Q19=makeQuery(id+"F1.imprint","IMPRINT",FACE,{"disambiguationData":[TD([[makeQuery(id+"F1.imprint","IMPRINT",EDGE,{"derivedFrom":sQuery(id+"F1.wireOp",EDGE,"E128.sketch_text.stroke-248")}),-1.0]])]});
            var Q20;
            Q20=makeQuery(id+"F1.imprint","IMPRINT",FACE,{"disambiguationData":[TD([[makeQuery(id+"F1.imprint","IMPRINT",EDGE,{"derivedFrom":sQuery(id+"F1.wireOp",EDGE,"E128.sketch_text.stroke-236")}),-1.0]])]});
            var Q21;
            Q21=makeQuery(id+"F1.imprint","IMPRINT",FACE,{"disambiguationData":[TD([[makeQuery(id+"F1.imprint","IMPRINT",EDGE,{"derivedFrom":sQuery(id+"F1.wireOp",EDGE,"E128.sketch_text.stroke-220")}),-1.0]])]});
            extrude(context, id + "F4", {"entities" : qUnion([Q0, Q1, Q2, Q3, Q4, Q5, Q6, Q7, Q8, Q9, Q10, Q11, Q12, Q13, Q14, Q15, Q16, Q17, Q18, Q19, Q20, Q21]), "depth" : 13 * mm, "offsetDistance" : 25 * mm});
        }
        {
            var Q0;
            Q0=makeQuery(id+"F2.opExtrude","SWEPT_BODY",BODY,{"disambiguationData":[OSD([sQuery(id+"F0.wireOp",EDGE,"E5.bottom"),sQuery(id+"F0.wireOp",EDGE,"E5.top"),sQuery(id+"F0.wireOp",EDGE,"E5.left"),sQuery(id+"F0.wireOp",EDGE,"E5.right"),sQuery(id+"F0.wireOp",EDGE,"E6.bottom"),sQuery(id+"F0.wireOp",EDGE,"E6.top"),sQuery(id+"F0.wireOp",EDGE,"E6.left"),sQuery(id+"F0.wireOp",EDGE,"E6.right"),sQuery(id+"F0.wireOp",EDGE,"E7"),sQuery(id+"F0.wireOp",EDGE,"E8"),sQuery(id+"F0.wireOp",EDGE,"E9"),sQuery(id+"F0.wireOp",EDGE,"E10.trimOffspring"),sQuery(id+"F0.wireOp",EDGE,"E11.trimOffspring"),sQuery(id+"F0.wireOp",EDGE,"E12.trimOffspring"),sQuery(id+"F0.wireOp",EDGE,"E13"),sQuery(id+"F0.wireOp",EDGE,"E14.trimOffspring"),sQuery(id+"F0.wireOp",EDGE,"E15.filletArc"),sQuery(id+"F0.wireOp",EDGE,"E16.filletArc"),sQuery(id+"F0.wireOp",EDGE,"E17.filletArc"),sQuery(id+"F0.wireOp",EDGE,"E18.filletArc"),sQuery(id+"F0.wireOp",EDGE,"E19.filletArc"),sQuery(id+"F0.wireOp",EDGE,"E20.filletArc"),sQuery(id+"F0.wireOp",EDGE,"E21.filletArc"),sQuery(id+"F0.wireOp",EDGE,"E22.filletArc")])]});
            var Q1;
            Q1=makeQuery(id+"F2.opExtrude","SWEPT_BODY",BODY,{"disambiguationData":[OSD([sQuery(id+"F1.wireOp",EDGE,"E44"),sQuery(id+"F1.wireOp",EDGE,"E45"),sQuery(id+"F1.wireOp",EDGE,"E46"),sQuery(id+"F1.wireOp",EDGE,"E125"),sQuery(id+"F1.wireOp",EDGE,"7oulb39c-XgtW-JnOE-ZCTZ-QdY41l89scCM"),sQuery(id+"F1.wireOp",EDGE,"E126")])]});
            var Q2;
            Q2=makeQuery(id+"F3.opExtrude","SWEPT_BODY",BODY,{"disambiguationData":[OSD([sQuery(id+"F1.wireOp",EDGE,"E23"),sQuery(id+"F1.wireOp",EDGE,"E34"),sQuery(id+"F1.wireOp",EDGE,"E35")])]});
            var Q3;
            Q3=makeQuery(id+"F3.opExtrude","SWEPT_BODY",BODY,{"disambiguationData":[OSD([sQuery(id+"F1.wireOp",EDGE,"E24"),sQuery(id+"F1.wireOp",EDGE,"E25"),sQuery(id+"F1.wireOp",EDGE,"E41.trimOffspring")])]});
            var Q4;
            Q4=makeQuery(id+"F3.opExtrude","SWEPT_BODY",BODY,{"disambiguationData":[OSD([sQuery(id+"F1.wireOp",EDGE,"E26"),sQuery(id+"F1.wireOp",EDGE,"E27"),sQuery(id+"F1.wireOp",EDGE,"E42.trimOffspring")])]});
            var Q5;
            Q5=makeQuery(id+"F3.opExtrude","SWEPT_BODY",BODY,{"disambiguationData":[OSD([sQuery(id+"F1.wireOp",EDGE,"E28"),sQuery(id+"F1.wireOp",EDGE,"E29"),sQuery(id+"F1.wireOp",EDGE,"E43.trimOffspring")])]});
            var Q6;
            Q6=makeQuery(id+"F3.opExtrude","SWEPT_BODY",BODY,{"disambiguationData":[OSD([sQuery(id+"F1.wireOp",EDGE,"E30"),sQuery(id+"F1.wireOp",EDGE,"E31"),sQuery(id+"F1.wireOp",EDGE,"E40.trimOffspring")])]});
            var Q7;
            Q7=makeQuery(id+"F3.opExtrude","SWEPT_BODY",BODY,{"disambiguationData":[OSD([sQuery(id+"F1.wireOp",EDGE,"E32"),sQuery(id+"F1.wireOp",EDGE,"E33"),sQuery(id+"F1.wireOp",EDGE,"E39.trimOffspring")])]});
            var Q8;
            Q8=makeQuery(id+"F3.opExtrude","SWEPT_BODY",BODY,{"disambiguationData":[OSD([sQuery(id+"F1.wireOp",EDGE,"E36"),sQuery(id+"F1.wireOp",EDGE,"E37"),sQuery(id+"F1.wireOp",EDGE,"E38.trimOffspring")])]});
            var Q9;
            Q9=makeQuery(id+"F3.opExtrude","SWEPT_BODY",BODY,{"disambiguationData":[OSD([sQuery(id+"F1.wireOp",EDGE,"E47"),sQuery(id+"F1.wireOp",EDGE,"E48"),sQuery(id+"F1.wireOp",EDGE,"E49"),sQuery(id+"F1.wireOp",EDGE,"E50"),sQuery(id+"F1.wireOp",EDGE,"E51"),sQuery(id+"F1.wireOp",EDGE,"E52"),sQuery(id+"F1.wireOp",EDGE,"E53"),sQuery(id+"F1.wireOp",EDGE,"E54"),sQuery(id+"F1.wireOp",EDGE,"E55"),sQuery(id+"F1.wireOp",EDGE,"E56"),sQuery(id+"F1.wireOp",EDGE,"E57")])]});
            var Q10;
            Q10=makeQuery(id+"F3.opExtrude","SWEPT_BODY",BODY,{"disambiguationData":[OSD([sQuery(id+"F1.wireOp",EDGE,"E58"),sQuery(id+"F1.wireOp",EDGE,"E59"),sQuery(id+"F1.wireOp",EDGE,"E60"),sQuery(id+"F1.wireOp",EDGE,"E61"),sQuery(id+"F1.wireOp",EDGE,"E62"),sQuery(id+"F1.wireOp",EDGE,"E63"),sQuery(id+"F1.wireOp",EDGE,"E64"),sQuery(id+"F1.wireOp",EDGE,"E65")])]});
            var Q11;
            Q11=makeQuery(id+"F3.opExtrude","SWEPT_BODY",BODY,{"disambiguationData":[OSD([sQuery(id+"F1.wireOp",EDGE,"E66"),sQuery(id+"F1.wireOp",EDGE,"E67"),sQuery(id+"F1.wireOp",EDGE,"E68"),sQuery(id+"F1.wireOp",EDGE,"E69"),sQuery(id+"F1.wireOp",EDGE,"E70"),sQuery(id+"F1.wireOp",EDGE,"E71"),sQuery(id+"F1.wireOp",EDGE,"E72"),sQuery(id+"F1.wireOp",EDGE,"E73"),sQuery(id+"F1.wireOp",EDGE,"E74"),sQuery(id+"F1.wireOp",EDGE,"E75"),sQuery(id+"F1.wireOp",EDGE,"E76"),sQuery(id+"F1.wireOp",EDGE,"E77")])]});
            var Q12;
            Q12=makeQuery(id+"F3.opExtrude","SWEPT_BODY",BODY,{"disambiguationData":[OSD([sQuery(id+"F1.wireOp",EDGE,"E78"),sQuery(id+"F1.wireOp",EDGE,"E79"),sQuery(id+"F1.wireOp",EDGE,"E80"),sQuery(id+"F1.wireOp",EDGE,"E81"),sQuery(id+"F1.wireOp",EDGE,"E82"),sQuery(id+"F1.wireOp",EDGE,"E83"),sQuery(id+"F1.wireOp",EDGE,"E84"),sQuery(id+"F1.wireOp",EDGE,"E85")])]});
            var Q13;
            Q13=makeQuery(id+"F3.opExtrude","SWEPT_BODY",BODY,{"disambiguationData":[OSD([sQuery(id+"F1.wireOp",EDGE,"E86"),sQuery(id+"F1.wireOp",EDGE,"E87"),sQuery(id+"F1.wireOp",EDGE,"E88"),sQuery(id+"F1.wireOp",EDGE,"E89"),sQuery(id+"F1.wireOp",EDGE,"E90"),sQuery(id+"F1.wireOp",EDGE,"E91"),sQuery(id+"F1.wireOp",EDGE,"E92"),sQuery(id+"F1.wireOp",EDGE,"E93"),sQuery(id+"F1.wireOp",EDGE,"E94"),sQuery(id+"F1.wireOp",EDGE,"E95"),sQuery(id+"F1.wireOp",EDGE,"E96"),sQuery(id+"F1.wireOp",EDGE,"E97")])]});
            var Q14;
            Q14=makeQuery(id+"F3.opExtrude","SWEPT_BODY",BODY,{"disambiguationData":[OSD([sQuery(id+"F1.wireOp",EDGE,"E98"),sQuery(id+"F1.wireOp",EDGE,"E99"),sQuery(id+"F1.wireOp",EDGE,"E100"),sQuery(id+"F1.wireOp",EDGE,"E101"),sQuery(id+"F1.wireOp",EDGE,"E102"),sQuery(id+"F1.wireOp",EDGE,"E103"),sQuery(id+"F1.wireOp",EDGE,"E112"),sQuery(id+"F1.wireOp",EDGE,"E113"),sQuery(id+"F1.wireOp",EDGE,"E114"),sQuery(id+"F1.wireOp",EDGE,"E127")])]});
            var Q15;
            Q15=makeQuery(id+"F3.opExtrude","SWEPT_BODY",BODY,{"disambiguationData":[OSD([sQuery(id+"F1.wireOp",EDGE,"E104"),sQuery(id+"F1.wireOp",EDGE,"E105"),sQuery(id+"F1.wireOp",EDGE,"E115"),sQuery(id+"F1.wireOp",EDGE,"E116")])]});
            var Q16;
            Q16=makeQuery(id+"F3.opExtrude","SWEPT_BODY",BODY,{"disambiguationData":[OSD([sQuery(id+"F1.wireOp",EDGE,"E106"),sQuery(id+"F1.wireOp",EDGE,"E107"),sQuery(id+"F1.wireOp",EDGE,"E108"),sQuery(id+"F1.wireOp",EDGE,"E109"),sQuery(id+"F1.wireOp",EDGE,"E110"),sQuery(id+"F1.wireOp",EDGE,"E111"),sQuery(id+"F1.wireOp",EDGE,"E117"),sQuery(id+"F1.wireOp",EDGE,"E118"),sQuery(id+"F1.wireOp",EDGE,"E119"),sQuery(id+"F1.wireOp",EDGE,"E120"),sQuery(id+"F1.wireOp",EDGE,"E121"),sQuery(id+"F1.wireOp",EDGE,"E122"),sQuery(id+"F1.wireOp",EDGE,"E123")])]});
            var Q17;
            Q17=makeQuery(id+"F3.opExtrude","SWEPT_BODY",BODY,{"disambiguationData":[OSD([sQuery(id+"F1.wireOp",EDGE,"E124.sketch_text.stroke-0"),sQuery(id+"F1.wireOp",EDGE,"E124.sketch_text.stroke-1"),sQuery(id+"F1.wireOp",EDGE,"E124.sketch_text.stroke-2"),sQuery(id+"F1.wireOp",EDGE,"E124.sketch_text.stroke-3"),sQuery(id+"F1.wireOp",EDGE,"E124.sketch_text.stroke-4"),sQuery(id+"F1.wireOp",EDGE,"E124.sketch_text.stroke-5")])]});
            var Q18;
            Q18=makeQuery(id+"F3.opExtrude","SWEPT_BODY",BODY,{"disambiguationData":[OSD([sQuery(id+"F1.wireOp",EDGE,"E124.sketch_text.stroke-6"),sQuery(id+"F1.wireOp",EDGE,"E124.sketch_text.stroke-7"),sQuery(id+"F1.wireOp",EDGE,"E124.sketch_text.stroke-8"),sQuery(id+"F1.wireOp",EDGE,"E124.sketch_text.stroke-9"),sQuery(id+"F1.wireOp",EDGE,"E124.sketch_text.stroke-10"),sQuery(id+"F1.wireOp",EDGE,"E124.sketch_text.stroke-11"),sQuery(id+"F1.wireOp",EDGE,"E124.sketch_text.stroke-12"),sQuery(id+"F1.wireOp",EDGE,"E124.sketch_text.stroke-13"),sQuery(id+"F1.wireOp",EDGE,"E124.sketch_text.stroke-14"),sQuery(id+"F1.wireOp",EDGE,"E124.sketch_text.stroke-15"),sQuery(id+"F1.wireOp",EDGE,"E124.sketch_text.stroke-16"),sQuery(id+"F1.wireOp",EDGE,"E124.sketch_text.stroke-17")])]});
            var Q19;
            Q19=makeQuery(id+"F3.opExtrude","SWEPT_BODY",BODY,{"disambiguationData":[OSD([sQuery(id+"F1.wireOp",EDGE,"E124.sketch_text.stroke-18"),sQuery(id+"F1.wireOp",EDGE,"E124.sketch_text.stroke-19"),sQuery(id+"F1.wireOp",EDGE,"E124.sketch_text.stroke-20"),sQuery(id+"F1.wireOp",EDGE,"E124.sketch_text.stroke-21"),sQuery(id+"F1.wireOp",EDGE,"E124.sketch_text.stroke-22"),sQuery(id+"F1.wireOp",EDGE,"E124.sketch_text.stroke-23"),sQuery(id+"F1.wireOp",EDGE,"E124.sketch_text.stroke-24"),sQuery(id+"F1.wireOp",EDGE,"E124.sketch_text.stroke-25"),sQuery(id+"F1.wireOp",EDGE,"E124.sketch_text.stroke-26"),sQuery(id+"F1.wireOp",EDGE,"E124.sketch_text.stroke-27"),sQuery(id+"F1.wireOp",EDGE,"E124.sketch_text.stroke-28"),sQuery(id+"F1.wireOp",EDGE,"E124.sketch_text.stroke-29"),sQuery(id+"F1.wireOp",EDGE,"E124.sketch_text.stroke-30"),sQuery(id+"F1.wireOp",EDGE,"E124.sketch_text.stroke-31"),sQuery(id+"F1.wireOp",EDGE,"E124.sketch_text.stroke-32"),sQuery(id+"F1.wireOp",EDGE,"E124.sketch_text.stroke-33"),sQuery(id+"F1.wireOp",EDGE,"E124.sketch_text.stroke-34"),sQuery(id+"F1.wireOp",EDGE,"E124.sketch_text.stroke-35"),sQuery(id+"F1.wireOp",EDGE,"E124.sketch_text.stroke-36"),sQuery(id+"F1.wireOp",EDGE,"E124.sketch_text.stroke-37"),sQuery(id+"F1.wireOp",EDGE,"E124.sketch_text.stroke-38"),sQuery(id+"F1.wireOp",EDGE,"E124.sketch_text.stroke-39"),sQuery(id+"F1.wireOp",EDGE,"E124.sketch_text.stroke-40"),sQuery(id+"F1.wireOp",EDGE,"E124.sketch_text.stroke-41"),sQuery(id+"F1.wireOp",EDGE,"E124.sketch_text.stroke-42")])]});
            var Q20;
            Q20=makeQuery(id+"F3.opExtrude","SWEPT_BODY",BODY,{"disambiguationData":[OSD([sQuery(id+"F1.wireOp",EDGE,"E124.sketch_text.stroke-43"),sQuery(id+"F1.wireOp",EDGE,"E124.sketch_text.stroke-44"),sQuery(id+"F1.wireOp",EDGE,"E124.sketch_text.stroke-45"),sQuery(id+"F1.wireOp",EDGE,"E124.sketch_text.stroke-46"),sQuery(id+"F1.wireOp",EDGE,"E124.sketch_text.stroke-47"),sQuery(id+"F1.wireOp",EDGE,"E124.sketch_text.stroke-48"),sQuery(id+"F1.wireOp",EDGE,"E124.sketch_text.stroke-49"),sQuery(id+"F1.wireOp",EDGE,"E124.sketch_text.stroke-50"),sQuery(id+"F1.wireOp",EDGE,"E124.sketch_text.stroke-51"),sQuery(id+"F1.wireOp",EDGE,"E124.sketch_text.stroke-52"),sQuery(id+"F1.wireOp",EDGE,"E124.sketch_text.stroke-53"),sQuery(id+"F1.wireOp",EDGE,"E124.sketch_text.stroke-54"),sQuery(id+"F1.wireOp",EDGE,"E124.sketch_text.stroke-55"),sQuery(id+"F1.wireOp",EDGE,"E124.sketch_text.stroke-56")])]});
            var Q21;
            Q21=makeQuery(id+"F3.opExtrude","SWEPT_BODY",BODY,{"disambiguationData":[OSD([sQuery(id+"F1.wireOp",EDGE,"E124.sketch_text.stroke-57"),sQuery(id+"F1.wireOp",EDGE,"E124.sketch_text.stroke-58"),sQuery(id+"F1.wireOp",EDGE,"E124.sketch_text.stroke-59"),sQuery(id+"F1.wireOp",EDGE,"E124.sketch_text.stroke-60"),sQuery(id+"F1.wireOp",EDGE,"E124.sketch_text.stroke-61"),sQuery(id+"F1.wireOp",EDGE,"E124.sketch_text.stroke-62"),sQuery(id+"F1.wireOp",EDGE,"E124.sketch_text.stroke-63"),sQuery(id+"F1.wireOp",EDGE,"E124.sketch_text.stroke-64"),sQuery(id+"F1.wireOp",EDGE,"E124.sketch_text.stroke-65"),sQuery(id+"F1.wireOp",EDGE,"E124.sketch_text.stroke-66"),sQuery(id+"F1.wireOp",EDGE,"E124.sketch_text.stroke-67"),sQuery(id+"F1.wireOp",EDGE,"E124.sketch_text.stroke-68"),sQuery(id+"F1.wireOp",EDGE,"E124.sketch_text.stroke-69"),sQuery(id+"F1.wireOp",EDGE,"E124.sketch_text.stroke-70"),sQuery(id+"F1.wireOp",EDGE,"E124.sketch_text.stroke-71"),sQuery(id+"F1.wireOp",EDGE,"E124.sketch_text.stroke-72"),sQuery(id+"F1.wireOp",EDGE,"E124.sketch_text.stroke-73"),sQuery(id+"F1.wireOp",EDGE,"E124.sketch_text.stroke-74"),sQuery(id+"F1.wireOp",EDGE,"E124.sketch_text.stroke-75")])]});
            var Q22;
            Q22=makeQuery(id+"F3.opExtrude","SWEPT_BODY",BODY,{"disambiguationData":[OSD([sQuery(id+"F1.wireOp",EDGE,"E124.sketch_text.stroke-76"),sQuery(id+"F1.wireOp",EDGE,"E124.sketch_text.stroke-77"),sQuery(id+"F1.wireOp",EDGE,"E124.sketch_text.stroke-78"),sQuery(id+"F1.wireOp",EDGE,"E124.sketch_text.stroke-79"),sQuery(id+"F1.wireOp",EDGE,"E124.sketch_text.stroke-80"),sQuery(id+"F1.wireOp",EDGE,"E124.sketch_text.stroke-81"),sQuery(id+"F1.wireOp",EDGE,"E124.sketch_text.stroke-82"),sQuery(id+"F1.wireOp",EDGE,"E124.sketch_text.stroke-83"),sQuery(id+"F1.wireOp",EDGE,"E124.sketch_text.stroke-84"),sQuery(id+"F1.wireOp",EDGE,"E124.sketch_text.stroke-85"),sQuery(id+"F1.wireOp",EDGE,"E124.sketch_text.stroke-86"),sQuery(id+"F1.wireOp",EDGE,"E124.sketch_text.stroke-87")])]});
            var Q23;
            Q23=makeQuery(id+"F3.opExtrude","SWEPT_BODY",BODY,{"disambiguationData":[OSD([sQuery(id+"F1.wireOp",EDGE,"E124.sketch_text.stroke-88"),sQuery(id+"F1.wireOp",EDGE,"E124.sketch_text.stroke-89"),sQuery(id+"F1.wireOp",EDGE,"E124.sketch_text.stroke-90"),sQuery(id+"F1.wireOp",EDGE,"E124.sketch_text.stroke-91"),sQuery(id+"F1.wireOp",EDGE,"E124.sketch_text.stroke-92"),sQuery(id+"F1.wireOp",EDGE,"E124.sketch_text.stroke-93"),sQuery(id+"F1.wireOp",EDGE,"E124.sketch_text.stroke-94"),sQuery(id+"F1.wireOp",EDGE,"E124.sketch_text.stroke-95")])]});
            var Q24;
            Q24=makeQuery(id+"F3.opExtrude","SWEPT_BODY",BODY,{"disambiguationData":[OSD([sQuery(id+"F1.wireOp",EDGE,"E124.sketch_text.stroke-96"),sQuery(id+"F1.wireOp",EDGE,"E124.sketch_text.stroke-97"),sQuery(id+"F1.wireOp",EDGE,"E124.sketch_text.stroke-98"),sQuery(id+"F1.wireOp",EDGE,"E124.sketch_text.stroke-99"),sQuery(id+"F1.wireOp",EDGE,"E124.sketch_text.stroke-100"),sQuery(id+"F1.wireOp",EDGE,"E124.sketch_text.stroke-101"),sQuery(id+"F1.wireOp",EDGE,"E124.sketch_text.stroke-102"),sQuery(id+"F1.wireOp",EDGE,"E124.sketch_text.stroke-103"),sQuery(id+"F1.wireOp",EDGE,"E124.sketch_text.stroke-104"),sQuery(id+"F1.wireOp",EDGE,"E124.sketch_text.stroke-105"),sQuery(id+"F1.wireOp",EDGE,"E124.sketch_text.stroke-106"),sQuery(id+"F1.wireOp",EDGE,"E124.sketch_text.stroke-107"),sQuery(id+"F1.wireOp",EDGE,"E124.sketch_text.stroke-108"),sQuery(id+"F1.wireOp",EDGE,"E124.sketch_text.stroke-109")])]});
            var Q25;
            Q25=makeQuery(id+"F3.opExtrude","SWEPT_BODY",BODY,{"disambiguationData":[OSD([sQuery(id+"F1.wireOp",EDGE,"E124.sketch_text.stroke-110"),sQuery(id+"F1.wireOp",EDGE,"E124.sketch_text.stroke-111"),sQuery(id+"F1.wireOp",EDGE,"E124.sketch_text.stroke-112"),sQuery(id+"F1.wireOp",EDGE,"E124.sketch_text.stroke-113"),sQuery(id+"F1.wireOp",EDGE,"E124.sketch_text.stroke-114"),sQuery(id+"F1.wireOp",EDGE,"E124.sketch_text.stroke-115"),sQuery(id+"F1.wireOp",EDGE,"E124.sketch_text.stroke-116"),sQuery(id+"F1.wireOp",EDGE,"E124.sketch_text.stroke-117"),sQuery(id+"F1.wireOp",EDGE,"E124.sketch_text.stroke-118"),sQuery(id+"F1.wireOp",EDGE,"E124.sketch_text.stroke-119"),sQuery(id+"F1.wireOp",EDGE,"E124.sketch_text.stroke-120"),sQuery(id+"F1.wireOp",EDGE,"E124.sketch_text.stroke-121"),sQuery(id+"F1.wireOp",EDGE,"E124.sketch_text.stroke-122"),sQuery(id+"F1.wireOp",EDGE,"E124.sketch_text.stroke-123"),sQuery(id+"F1.wireOp",EDGE,"E124.sketch_text.stroke-124"),sQuery(id+"F1.wireOp",EDGE,"E124.sketch_text.stroke-125"),sQuery(id+"F1.wireOp",EDGE,"E124.sketch_text.stroke-126"),sQuery(id+"F1.wireOp",EDGE,"E124.sketch_text.stroke-127"),sQuery(id+"F1.wireOp",EDGE,"E124.sketch_text.stroke-128")])]});
            var Q26;
            Q26=makeQuery(id+"F3.opExtrude","SWEPT_BODY",BODY,{"disambiguationData":[OSD([sQuery(id+"F1.wireOp",EDGE,"E124.sketch_text.stroke-129"),sQuery(id+"F1.wireOp",EDGE,"E124.sketch_text.stroke-130"),sQuery(id+"F1.wireOp",EDGE,"E124.sketch_text.stroke-131"),sQuery(id+"F1.wireOp",EDGE,"E124.sketch_text.stroke-132"),sQuery(id+"F1.wireOp",EDGE,"E124.sketch_text.stroke-133"),sQuery(id+"F1.wireOp",EDGE,"E124.sketch_text.stroke-134"),sQuery(id+"F1.wireOp",EDGE,"E124.sketch_text.stroke-135"),sQuery(id+"F1.wireOp",EDGE,"E124.sketch_text.stroke-136"),sQuery(id+"F1.wireOp",EDGE,"E124.sketch_text.stroke-137"),sQuery(id+"F1.wireOp",EDGE,"E124.sketch_text.stroke-138"),sQuery(id+"F1.wireOp",EDGE,"E124.sketch_text.stroke-139"),sQuery(id+"F1.wireOp",EDGE,"E124.sketch_text.stroke-140")])]});
            var Q27;
            Q27=makeQuery(id+"F3.opExtrude","SWEPT_BODY",BODY,{"disambiguationData":[OSD([sQuery(id+"F1.wireOp",EDGE,"E124.sketch_text.stroke-141"),sQuery(id+"F1.wireOp",EDGE,"E124.sketch_text.stroke-142"),sQuery(id+"F1.wireOp",EDGE,"E124.sketch_text.stroke-143"),sQuery(id+"F1.wireOp",EDGE,"E124.sketch_text.stroke-144"),sQuery(id+"F1.wireOp",EDGE,"E124.sketch_text.stroke-145"),sQuery(id+"F1.wireOp",EDGE,"E124.sketch_text.stroke-146"),sQuery(id+"F1.wireOp",EDGE,"E124.sketch_text.stroke-147"),sQuery(id+"F1.wireOp",EDGE,"E124.sketch_text.stroke-148"),sQuery(id+"F1.wireOp",EDGE,"E124.sketch_text.stroke-149"),sQuery(id+"F1.wireOp",EDGE,"E124.sketch_text.stroke-150"),sQuery(id+"F1.wireOp",EDGE,"E124.sketch_text.stroke-151"),sQuery(id+"F1.wireOp",EDGE,"E124.sketch_text.stroke-152")])]});
            var Q28;
            Q28=makeQuery(id+"F3.opExtrude","SWEPT_BODY",BODY,{"disambiguationData":[OSD([sQuery(id+"F1.wireOp",EDGE,"E124.sketch_text.stroke-153"),sQuery(id+"F1.wireOp",EDGE,"E124.sketch_text.stroke-154"),sQuery(id+"F1.wireOp",EDGE,"E124.sketch_text.stroke-155"),sQuery(id+"F1.wireOp",EDGE,"E124.sketch_text.stroke-156"),sQuery(id+"F1.wireOp",EDGE,"E124.sketch_text.stroke-157"),sQuery(id+"F1.wireOp",EDGE,"E124.sketch_text.stroke-158"),sQuery(id+"F1.wireOp",EDGE,"E124.sketch_text.stroke-159"),sQuery(id+"F1.wireOp",EDGE,"E124.sketch_text.stroke-160"),sQuery(id+"F1.wireOp",EDGE,"E124.sketch_text.stroke-161"),sQuery(id+"F1.wireOp",EDGE,"E124.sketch_text.stroke-162"),sQuery(id+"F1.wireOp",EDGE,"E124.sketch_text.stroke-163"),sQuery(id+"F1.wireOp",EDGE,"E124.sketch_text.stroke-164"),sQuery(id+"F1.wireOp",EDGE,"E124.sketch_text.stroke-165"),sQuery(id+"F1.wireOp",EDGE,"E124.sketch_text.stroke-166"),sQuery(id+"F1.wireOp",EDGE,"E124.sketch_text.stroke-167"),sQuery(id+"F1.wireOp",EDGE,"E124.sketch_text.stroke-168"),sQuery(id+"F1.wireOp",EDGE,"E124.sketch_text.stroke-169"),sQuery(id+"F1.wireOp",EDGE,"E124.sketch_text.stroke-170"),sQuery(id+"F1.wireOp",EDGE,"E124.sketch_text.stroke-171"),sQuery(id+"F1.wireOp",EDGE,"E124.sketch_text.stroke-172"),sQuery(id+"F1.wireOp",EDGE,"E124.sketch_text.stroke-173"),sQuery(id+"F1.wireOp",EDGE,"E124.sketch_text.stroke-174"),sQuery(id+"F1.wireOp",EDGE,"E124.sketch_text.stroke-175"),sQuery(id+"F1.wireOp",EDGE,"E124.sketch_text.stroke-176"),sQuery(id+"F1.wireOp",EDGE,"E124.sketch_text.stroke-177"),sQuery(id+"F1.wireOp",EDGE,"E124.sketch_text.stroke-178"),sQuery(id+"F1.wireOp",EDGE,"E124.sketch_text.stroke-179"),sQuery(id+"F1.wireOp",EDGE,"E124.sketch_text.stroke-180")])]});
            var Q29;
            Q29=makeQuery(id+"F4.opExtrude","SWEPT_BODY",BODY,{"disambiguationData":[OSD([sQuery(id+"F1.wireOp",EDGE,"E128.sketch_text.stroke-0"),sQuery(id+"F1.wireOp",EDGE,"E128.sketch_text.stroke-1"),sQuery(id+"F1.wireOp",EDGE,"E128.sketch_text.stroke-2"),sQuery(id+"F1.wireOp",EDGE,"E128.sketch_text.stroke-3"),sQuery(id+"F1.wireOp",EDGE,"E128.sketch_text.stroke-4"),sQuery(id+"F1.wireOp",EDGE,"E128.sketch_text.stroke-5"),sQuery(id+"F1.wireOp",EDGE,"E128.sketch_text.stroke-6"),sQuery(id+"F1.wireOp",EDGE,"E128.sketch_text.stroke-7"),sQuery(id+"F1.wireOp",EDGE,"E128.sketch_text.stroke-8"),sQuery(id+"F1.wireOp",EDGE,"E128.sketch_text.stroke-9"),sQuery(id+"F1.wireOp",EDGE,"E128.sketch_text.stroke-10"),sQuery(id+"F1.wireOp",EDGE,"E128.sketch_text.stroke-11"),sQuery(id+"F1.wireOp",EDGE,"E128.sketch_text.stroke-12"),sQuery(id+"F1.wireOp",EDGE,"E128.sketch_text.stroke-13"),sQuery(id+"F1.wireOp",EDGE,"E128.sketch_text.stroke-14"),sQuery(id+"F1.wireOp",EDGE,"E128.sketch_text.stroke-15"),sQuery(id+"F1.wireOp",EDGE,"E128.sketch_text.stroke-16"),sQuery(id+"F1.wireOp",EDGE,"E128.sketch_text.stroke-17"),sQuery(id+"F1.wireOp",EDGE,"E128.sketch_text.stroke-18"),sQuery(id+"F1.wireOp",EDGE,"E128.sketch_text.stroke-19"),sQuery(id+"F1.wireOp",EDGE,"E128.sketch_text.stroke-20"),sQuery(id+"F1.wireOp",EDGE,"E128.sketch_text.stroke-21"),sQuery(id+"F1.wireOp",EDGE,"E128.sketch_text.stroke-22"),sQuery(id+"F1.wireOp",EDGE,"E128.sketch_text.stroke-23")])]});
            var Q30;
            Q30=makeQuery(id+"F4.opExtrude","SWEPT_BODY",BODY,{"disambiguationData":[OSD([sQuery(id+"F1.wireOp",EDGE,"E128.sketch_text.stroke-24"),sQuery(id+"F1.wireOp",EDGE,"E128.sketch_text.stroke-25"),sQuery(id+"F1.wireOp",EDGE,"E128.sketch_text.stroke-26"),sQuery(id+"F1.wireOp",EDGE,"E128.sketch_text.stroke-27"),sQuery(id+"F1.wireOp",EDGE,"E128.sketch_text.stroke-28"),sQuery(id+"F1.wireOp",EDGE,"E128.sketch_text.stroke-29"),sQuery(id+"F1.wireOp",EDGE,"E128.sketch_text.stroke-30"),sQuery(id+"F1.wireOp",EDGE,"E128.sketch_text.stroke-31"),sQuery(id+"F1.wireOp",EDGE,"E128.sketch_text.stroke-32"),sQuery(id+"F1.wireOp",EDGE,"E128.sketch_text.stroke-33"),sQuery(id+"F1.wireOp",EDGE,"E128.sketch_text.stroke-34"),sQuery(id+"F1.wireOp",EDGE,"E128.sketch_text.stroke-35"),sQuery(id+"F1.wireOp",EDGE,"E128.sketch_text.stroke-36"),sQuery(id+"F1.wireOp",EDGE,"E128.sketch_text.stroke-37"),sQuery(id+"F1.wireOp",EDGE,"E128.sketch_text.stroke-38"),sQuery(id+"F1.wireOp",EDGE,"E128.sketch_text.stroke-39")])]});
            var Q31;
            Q31=makeQuery(id+"F4.opExtrude","SWEPT_BODY",BODY,{"disambiguationData":[OSD([sQuery(id+"F1.wireOp",EDGE,"E128.sketch_text.stroke-40"),sQuery(id+"F1.wireOp",EDGE,"E128.sketch_text.stroke-41"),sQuery(id+"F1.wireOp",EDGE,"E128.sketch_text.stroke-42"),sQuery(id+"F1.wireOp",EDGE,"E128.sketch_text.stroke-43"),sQuery(id+"F1.wireOp",EDGE,"E128.sketch_text.stroke-44"),sQuery(id+"F1.wireOp",EDGE,"E128.sketch_text.stroke-45"),sQuery(id+"F1.wireOp",EDGE,"E128.sketch_text.stroke-46"),sQuery(id+"F1.wireOp",EDGE,"E128.sketch_text.stroke-47"),sQuery(id+"F1.wireOp",EDGE,"E128.sketch_text.stroke-48"),sQuery(id+"F1.wireOp",EDGE,"E128.sketch_text.stroke-49"),sQuery(id+"F1.wireOp",EDGE,"E128.sketch_text.stroke-50"),sQuery(id+"F1.wireOp",EDGE,"E128.sketch_text.stroke-51"),sQuery(id+"F1.wireOp",EDGE,"E128.sketch_text.stroke-52")])]});
            var Q32;
            Q32=makeQuery(id+"F4.opExtrude","SWEPT_BODY",BODY,{"disambiguationData":[OSD([sQuery(id+"F1.wireOp",EDGE,"E128.sketch_text.stroke-53"),sQuery(id+"F1.wireOp",EDGE,"E128.sketch_text.stroke-54"),sQuery(id+"F1.wireOp",EDGE,"E128.sketch_text.stroke-55"),sQuery(id+"F1.wireOp",EDGE,"E128.sketch_text.stroke-56"),sQuery(id+"F1.wireOp",EDGE,"E128.sketch_text.stroke-57"),sQuery(id+"F1.wireOp",EDGE,"E128.sketch_text.stroke-58"),sQuery(id+"F1.wireOp",EDGE,"E128.sketch_text.stroke-59"),sQuery(id+"F1.wireOp",EDGE,"E128.sketch_text.stroke-60"),sQuery(id+"F1.wireOp",EDGE,"E128.sketch_text.stroke-61"),sQuery(id+"F1.wireOp",EDGE,"E128.sketch_text.stroke-62"),sQuery(id+"F1.wireOp",EDGE,"E128.sketch_text.stroke-63"),sQuery(id+"F1.wireOp",EDGE,"E128.sketch_text.stroke-64"),sQuery(id+"F1.wireOp",EDGE,"E128.sketch_text.stroke-65"),sQuery(id+"F1.wireOp",EDGE,"E128.sketch_text.stroke-66")])]});
            var Q33;
            Q33=makeQuery(id+"F4.opExtrude","SWEPT_BODY",BODY,{"disambiguationData":[OSD([sQuery(id+"F1.wireOp",EDGE,"E128.sketch_text.stroke-67"),sQuery(id+"F1.wireOp",EDGE,"E128.sketch_text.stroke-68"),sQuery(id+"F1.wireOp",EDGE,"E128.sketch_text.stroke-69"),sQuery(id+"F1.wireOp",EDGE,"E128.sketch_text.stroke-70"),sQuery(id+"F1.wireOp",EDGE,"E128.sketch_text.stroke-71"),sQuery(id+"F1.wireOp",EDGE,"E128.sketch_text.stroke-72"),sQuery(id+"F1.wireOp",EDGE,"E128.sketch_text.stroke-73"),sQuery(id+"F1.wireOp",EDGE,"E128.sketch_text.stroke-74")])]});
            var Q34;
            Q34=makeQuery(id+"F4.opExtrude","SWEPT_BODY",BODY,{"disambiguationData":[OSD([sQuery(id+"F1.wireOp",EDGE,"E128.sketch_text.stroke-75"),sQuery(id+"F1.wireOp",EDGE,"E128.sketch_text.stroke-76"),sQuery(id+"F1.wireOp",EDGE,"E128.sketch_text.stroke-77"),sQuery(id+"F1.wireOp",EDGE,"E128.sketch_text.stroke-78"),sQuery(id+"F1.wireOp",EDGE,"E128.sketch_text.stroke-79"),sQuery(id+"F1.wireOp",EDGE,"E128.sketch_text.stroke-80"),sQuery(id+"F1.wireOp",EDGE,"E128.sketch_text.stroke-81"),sQuery(id+"F1.wireOp",EDGE,"E128.sketch_text.stroke-82"),sQuery(id+"F1.wireOp",EDGE,"E128.sketch_text.stroke-83"),sQuery(id+"F1.wireOp",EDGE,"E128.sketch_text.stroke-84"),sQuery(id+"F1.wireOp",EDGE,"E128.sketch_text.stroke-85"),sQuery(id+"F1.wireOp",EDGE,"E128.sketch_text.stroke-86"),sQuery(id+"F1.wireOp",EDGE,"E128.sketch_text.stroke-87"),sQuery(id+"F1.wireOp",EDGE,"E128.sketch_text.stroke-88"),sQuery(id+"F1.wireOp",EDGE,"E128.sketch_text.stroke-89"),sQuery(id+"F1.wireOp",EDGE,"E128.sketch_text.stroke-90")])]});
            var Q35;
            Q35=makeQuery(id+"F4.opExtrude","SWEPT_BODY",BODY,{"disambiguationData":[OSD([sQuery(id+"F1.wireOp",EDGE,"E128.sketch_text.stroke-91"),sQuery(id+"F1.wireOp",EDGE,"E128.sketch_text.stroke-92"),sQuery(id+"F1.wireOp",EDGE,"E128.sketch_text.stroke-93"),sQuery(id+"F1.wireOp",EDGE,"E128.sketch_text.stroke-94"),sQuery(id+"F1.wireOp",EDGE,"E128.sketch_text.stroke-95"),sQuery(id+"F1.wireOp",EDGE,"E128.sketch_text.stroke-96"),sQuery(id+"F1.wireOp",EDGE,"E128.sketch_text.stroke-97"),sQuery(id+"F1.wireOp",EDGE,"E128.sketch_text.stroke-98"),sQuery(id+"F1.wireOp",EDGE,"E128.sketch_text.stroke-99"),sQuery(id+"F1.wireOp",EDGE,"E128.sketch_text.stroke-100"),sQuery(id+"F1.wireOp",EDGE,"E128.sketch_text.stroke-101"),sQuery(id+"F1.wireOp",EDGE,"E128.sketch_text.stroke-102"),sQuery(id+"F1.wireOp",EDGE,"E128.sketch_text.stroke-103"),sQuery(id+"F1.wireOp",EDGE,"E128.sketch_text.stroke-104"),sQuery(id+"F1.wireOp",EDGE,"E128.sketch_text.stroke-105"),sQuery(id+"F1.wireOp",EDGE,"E128.sketch_text.stroke-106"),sQuery(id+"F1.wireOp",EDGE,"E128.sketch_text.stroke-107"),sQuery(id+"F1.wireOp",EDGE,"E128.sketch_text.stroke-108"),sQuery(id+"F1.wireOp",EDGE,"E128.sketch_text.stroke-109")])]});
            var Q36;
            Q36=makeQuery(id+"F4.opExtrude","SWEPT_BODY",BODY,{"disambiguationData":[OSD([sQuery(id+"F1.wireOp",EDGE,"E128.sketch_text.stroke-110"),sQuery(id+"F1.wireOp",EDGE,"E128.sketch_text.stroke-111"),sQuery(id+"F1.wireOp",EDGE,"E128.sketch_text.stroke-112"),sQuery(id+"F1.wireOp",EDGE,"E128.sketch_text.stroke-113"),sQuery(id+"F1.wireOp",EDGE,"E128.sketch_text.stroke-114"),sQuery(id+"F1.wireOp",EDGE,"E128.sketch_text.stroke-115"),sQuery(id+"F1.wireOp",EDGE,"E128.sketch_text.stroke-116"),sQuery(id+"F1.wireOp",EDGE,"E128.sketch_text.stroke-117")])]});
            var Q37;
            Q37=makeQuery(id+"F4.opExtrude","SWEPT_BODY",BODY,{"disambiguationData":[OSD([sQuery(id+"F1.wireOp",EDGE,"E128.sketch_text.stroke-118"),sQuery(id+"F1.wireOp",EDGE,"E128.sketch_text.stroke-119"),sQuery(id+"F1.wireOp",EDGE,"E128.sketch_text.stroke-120"),sQuery(id+"F1.wireOp",EDGE,"E128.sketch_text.stroke-121"),sQuery(id+"F1.wireOp",EDGE,"E128.sketch_text.stroke-122"),sQuery(id+"F1.wireOp",EDGE,"E128.sketch_text.stroke-123"),sQuery(id+"F1.wireOp",EDGE,"E128.sketch_text.stroke-124"),sQuery(id+"F1.wireOp",EDGE,"E128.sketch_text.stroke-125"),sQuery(id+"F1.wireOp",EDGE,"E128.sketch_text.stroke-126"),sQuery(id+"F1.wireOp",EDGE,"E128.sketch_text.stroke-127"),sQuery(id+"F1.wireOp",EDGE,"E128.sketch_text.stroke-128"),sQuery(id+"F1.wireOp",EDGE,"E128.sketch_text.stroke-129"),sQuery(id+"F1.wireOp",EDGE,"E128.sketch_text.stroke-130"),sQuery(id+"F1.wireOp",EDGE,"E128.sketch_text.stroke-131"),sQuery(id+"F1.wireOp",EDGE,"E128.sketch_text.stroke-132"),sQuery(id+"F1.wireOp",EDGE,"E128.sketch_text.stroke-133")])]});
            var Q38;
            Q38=makeQuery(id+"F4.opExtrude","SWEPT_BODY",BODY,{"disambiguationData":[OSD([sQuery(id+"F1.wireOp",EDGE,"E128.sketch_text.stroke-134"),sQuery(id+"F1.wireOp",EDGE,"E128.sketch_text.stroke-135"),sQuery(id+"F1.wireOp",EDGE,"E128.sketch_text.stroke-136"),sQuery(id+"F1.wireOp",EDGE,"E128.sketch_text.stroke-137"),sQuery(id+"F1.wireOp",EDGE,"E128.sketch_text.stroke-138"),sQuery(id+"F1.wireOp",EDGE,"E128.sketch_text.stroke-139"),sQuery(id+"F1.wireOp",EDGE,"E128.sketch_text.stroke-140"),sQuery(id+"F1.wireOp",EDGE,"E128.sketch_text.stroke-141"),sQuery(id+"F1.wireOp",EDGE,"E128.sketch_text.stroke-142"),sQuery(id+"F1.wireOp",EDGE,"E128.sketch_text.stroke-143"),sQuery(id+"F1.wireOp",EDGE,"E128.sketch_text.stroke-144"),sQuery(id+"F1.wireOp",EDGE,"E128.sketch_text.stroke-145"),sQuery(id+"F1.wireOp",EDGE,"E128.sketch_text.stroke-146"),sQuery(id+"F1.wireOp",EDGE,"E128.sketch_text.stroke-147")])]});
            var Q39;
            Q39=makeQuery(id+"F4.opExtrude","SWEPT_BODY",BODY,{"disambiguationData":[OSD([sQuery(id+"F1.wireOp",EDGE,"E128.sketch_text.stroke-148"),sQuery(id+"F1.wireOp",EDGE,"E128.sketch_text.stroke-149"),sQuery(id+"F1.wireOp",EDGE,"E128.sketch_text.stroke-150"),sQuery(id+"F1.wireOp",EDGE,"E128.sketch_text.stroke-151"),sQuery(id+"F1.wireOp",EDGE,"E128.sketch_text.stroke-152"),sQuery(id+"F1.wireOp",EDGE,"E128.sketch_text.stroke-153"),sQuery(id+"F1.wireOp",EDGE,"E128.sketch_text.stroke-154"),sQuery(id+"F1.wireOp",EDGE,"E128.sketch_text.stroke-155"),sQuery(id+"F1.wireOp",EDGE,"E128.sketch_text.stroke-156"),sQuery(id+"F1.wireOp",EDGE,"E128.sketch_text.stroke-157"),sQuery(id+"F1.wireOp",EDGE,"E128.sketch_text.stroke-158"),sQuery(id+"F1.wireOp",EDGE,"E128.sketch_text.stroke-159"),sQuery(id+"F1.wireOp",EDGE,"E128.sketch_text.stroke-160"),sQuery(id+"F1.wireOp",EDGE,"E128.sketch_text.stroke-161")])]});
            var Q40;
            Q40=makeQuery(id+"F4.opExtrude","SWEPT_BODY",BODY,{"disambiguationData":[OSD([sQuery(id+"F1.wireOp",EDGE,"E128.sketch_text.stroke-162"),sQuery(id+"F1.wireOp",EDGE,"E128.sketch_text.stroke-163"),sQuery(id+"F1.wireOp",EDGE,"E128.sketch_text.stroke-164"),sQuery(id+"F1.wireOp",EDGE,"E128.sketch_text.stroke-165"),sQuery(id+"F1.wireOp",EDGE,"E128.sketch_text.stroke-166"),sQuery(id+"F1.wireOp",EDGE,"E128.sketch_text.stroke-167"),sQuery(id+"F1.wireOp",EDGE,"E128.sketch_text.stroke-168"),sQuery(id+"F1.wireOp",EDGE,"E128.sketch_text.stroke-169"),sQuery(id+"F1.wireOp",EDGE,"E128.sketch_text.stroke-170"),sQuery(id+"F1.wireOp",EDGE,"E128.sketch_text.stroke-171"),sQuery(id+"F1.wireOp",EDGE,"E128.sketch_text.stroke-172"),sQuery(id+"F1.wireOp",EDGE,"E128.sketch_text.stroke-173")])]});
            var Q41;
            Q41=makeQuery(id+"F4.opExtrude","SWEPT_BODY",BODY,{"disambiguationData":[OSD([sQuery(id+"F1.wireOp",EDGE,"E128.sketch_text.stroke-174"),sQuery(id+"F1.wireOp",EDGE,"E128.sketch_text.stroke-175"),sQuery(id+"F1.wireOp",EDGE,"E128.sketch_text.stroke-176"),sQuery(id+"F1.wireOp",EDGE,"E128.sketch_text.stroke-177"),sQuery(id+"F1.wireOp",EDGE,"E128.sketch_text.stroke-178"),sQuery(id+"F1.wireOp",EDGE,"E128.sketch_text.stroke-179")])]});
            var Q42;
            Q42=makeQuery(id+"F4.opExtrude","SWEPT_BODY",BODY,{"disambiguationData":[OSD([sQuery(id+"F1.wireOp",EDGE,"E128.sketch_text.stroke-180"),sQuery(id+"F1.wireOp",EDGE,"E128.sketch_text.stroke-181"),sQuery(id+"F1.wireOp",EDGE,"E128.sketch_text.stroke-182"),sQuery(id+"F1.wireOp",EDGE,"E128.sketch_text.stroke-183")])]});
            var Q43;
            Q43=makeQuery(id+"F4.opExtrude","SWEPT_BODY",BODY,{"disambiguationData":[OSD([sQuery(id+"F1.wireOp",EDGE,"E128.sketch_text.stroke-184"),sQuery(id+"F1.wireOp",EDGE,"E128.sketch_text.stroke-185"),sQuery(id+"F1.wireOp",EDGE,"E128.sketch_text.stroke-186"),sQuery(id+"F1.wireOp",EDGE,"E128.sketch_text.stroke-187"),sQuery(id+"F1.wireOp",EDGE,"E128.sketch_text.stroke-188"),sQuery(id+"F1.wireOp",EDGE,"E128.sketch_text.stroke-189"),sQuery(id+"F1.wireOp",EDGE,"E128.sketch_text.stroke-190"),sQuery(id+"F1.wireOp",EDGE,"E128.sketch_text.stroke-191"),sQuery(id+"F1.wireOp",EDGE,"E128.sketch_text.stroke-192"),sQuery(id+"F1.wireOp",EDGE,"E128.sketch_text.stroke-193"),sQuery(id+"F1.wireOp",EDGE,"E128.sketch_text.stroke-194"),sQuery(id+"F1.wireOp",EDGE,"E128.sketch_text.stroke-195"),sQuery(id+"F1.wireOp",EDGE,"E128.sketch_text.stroke-196"),sQuery(id+"F1.wireOp",EDGE,"E128.sketch_text.stroke-197")])]});
            var Q44;
            Q44=makeQuery(id+"F4.opExtrude","SWEPT_BODY",BODY,{"disambiguationData":[OSD([sQuery(id+"F1.wireOp",EDGE,"E128.sketch_text.stroke-198"),sQuery(id+"F1.wireOp",EDGE,"E128.sketch_text.stroke-199"),sQuery(id+"F1.wireOp",EDGE,"E128.sketch_text.stroke-200"),sQuery(id+"F1.wireOp",EDGE,"E128.sketch_text.stroke-201"),sQuery(id+"F1.wireOp",EDGE,"E128.sketch_text.stroke-202"),sQuery(id+"F1.wireOp",EDGE,"E128.sketch_text.stroke-203"),sQuery(id+"F1.wireOp",EDGE,"E128.sketch_text.stroke-204"),sQuery(id+"F1.wireOp",EDGE,"E128.sketch_text.stroke-205"),sQuery(id+"F1.wireOp",EDGE,"E128.sketch_text.stroke-206"),sQuery(id+"F1.wireOp",EDGE,"E128.sketch_text.stroke-207"),sQuery(id+"F1.wireOp",EDGE,"E128.sketch_text.stroke-208"),sQuery(id+"F1.wireOp",EDGE,"E128.sketch_text.stroke-209"),sQuery(id+"F1.wireOp",EDGE,"E128.sketch_text.stroke-210"),sQuery(id+"F1.wireOp",EDGE,"E128.sketch_text.stroke-211"),sQuery(id+"F1.wireOp",EDGE,"E128.sketch_text.stroke-212"),sQuery(id+"F1.wireOp",EDGE,"E128.sketch_text.stroke-213"),sQuery(id+"F1.wireOp",EDGE,"E128.sketch_text.stroke-214"),sQuery(id+"F1.wireOp",EDGE,"E128.sketch_text.stroke-215"),sQuery(id+"F1.wireOp",EDGE,"E128.sketch_text.stroke-216"),sQuery(id+"F1.wireOp",EDGE,"E128.sketch_text.stroke-217"),sQuery(id+"F1.wireOp",EDGE,"E128.sketch_text.stroke-218"),sQuery(id+"F1.wireOp",EDGE,"E128.sketch_text.stroke-219")])]});
            var Q45;
            Q45=makeQuery(id+"F4.opExtrude","SWEPT_BODY",BODY,{"disambiguationData":[OSD([sQuery(id+"F1.wireOp",EDGE,"E128.sketch_text.stroke-220"),sQuery(id+"F1.wireOp",EDGE,"E128.sketch_text.stroke-221"),sQuery(id+"F1.wireOp",EDGE,"E128.sketch_text.stroke-222"),sQuery(id+"F1.wireOp",EDGE,"E128.sketch_text.stroke-223"),sQuery(id+"F1.wireOp",EDGE,"E128.sketch_text.stroke-224"),sQuery(id+"F1.wireOp",EDGE,"E128.sketch_text.stroke-225"),sQuery(id+"F1.wireOp",EDGE,"E128.sketch_text.stroke-226"),sQuery(id+"F1.wireOp",EDGE,"E128.sketch_text.stroke-227"),sQuery(id+"F1.wireOp",EDGE,"E128.sketch_text.stroke-228"),sQuery(id+"F1.wireOp",EDGE,"E128.sketch_text.stroke-229"),sQuery(id+"F1.wireOp",EDGE,"E128.sketch_text.stroke-230"),sQuery(id+"F1.wireOp",EDGE,"E128.sketch_text.stroke-231"),sQuery(id+"F1.wireOp",EDGE,"E128.sketch_text.stroke-232"),sQuery(id+"F1.wireOp",EDGE,"E128.sketch_text.stroke-233"),sQuery(id+"F1.wireOp",EDGE,"E128.sketch_text.stroke-234"),sQuery(id+"F1.wireOp",EDGE,"E128.sketch_text.stroke-235")])]});
            var Q46;
            Q46=makeQuery(id+"F4.opExtrude","SWEPT_BODY",BODY,{"disambiguationData":[OSD([sQuery(id+"F1.wireOp",EDGE,"E128.sketch_text.stroke-236"),sQuery(id+"F1.wireOp",EDGE,"E128.sketch_text.stroke-237"),sQuery(id+"F1.wireOp",EDGE,"E128.sketch_text.stroke-238"),sQuery(id+"F1.wireOp",EDGE,"E128.sketch_text.stroke-239"),sQuery(id+"F1.wireOp",EDGE,"E128.sketch_text.stroke-240"),sQuery(id+"F1.wireOp",EDGE,"E128.sketch_text.stroke-241"),sQuery(id+"F1.wireOp",EDGE,"E128.sketch_text.stroke-242"),sQuery(id+"F1.wireOp",EDGE,"E128.sketch_text.stroke-243"),sQuery(id+"F1.wireOp",EDGE,"E128.sketch_text.stroke-244"),sQuery(id+"F1.wireOp",EDGE,"E128.sketch_text.stroke-245"),sQuery(id+"F1.wireOp",EDGE,"E128.sketch_text.stroke-246"),sQuery(id+"F1.wireOp",EDGE,"E128.sketch_text.stroke-247")])]});
            var Q47;
            Q47=makeQuery(id+"F4.opExtrude","SWEPT_BODY",BODY,{"disambiguationData":[OSD([sQuery(id+"F1.wireOp",EDGE,"E128.sketch_text.stroke-248"),sQuery(id+"F1.wireOp",EDGE,"E128.sketch_text.stroke-249"),sQuery(id+"F1.wireOp",EDGE,"E128.sketch_text.stroke-250"),sQuery(id+"F1.wireOp",EDGE,"E128.sketch_text.stroke-251"),sQuery(id+"F1.wireOp",EDGE,"E128.sketch_text.stroke-252"),sQuery(id+"F1.wireOp",EDGE,"E128.sketch_text.stroke-253"),sQuery(id+"F1.wireOp",EDGE,"E128.sketch_text.stroke-254"),sQuery(id+"F1.wireOp",EDGE,"E128.sketch_text.stroke-255"),sQuery(id+"F1.wireOp",EDGE,"E128.sketch_text.stroke-256"),sQuery(id+"F1.wireOp",EDGE,"E128.sketch_text.stroke-257")])]});
            var Q48;
            Q48=makeQuery(id+"F4.opExtrude","SWEPT_BODY",BODY,{"disambiguationData":[OSD([sQuery(id+"F1.wireOp",EDGE,"E128.sketch_text.stroke-258"),sQuery(id+"F1.wireOp",EDGE,"E128.sketch_text.stroke-259"),sQuery(id+"F1.wireOp",EDGE,"E128.sketch_text.stroke-260"),sQuery(id+"F1.wireOp",EDGE,"E128.sketch_text.stroke-261")])]});
            var Q49;
            Q49=makeQuery(id+"F4.opExtrude","SWEPT_BODY",BODY,{"disambiguationData":[OSD([sQuery(id+"F1.wireOp",EDGE,"E128.sketch_text.stroke-262"),sQuery(id+"F1.wireOp",EDGE,"E128.sketch_text.stroke-263"),sQuery(id+"F1.wireOp",EDGE,"E128.sketch_text.stroke-264"),sQuery(id+"F1.wireOp",EDGE,"E128.sketch_text.stroke-265"),sQuery(id+"F1.wireOp",EDGE,"E128.sketch_text.stroke-266"),sQuery(id+"F1.wireOp",EDGE,"E128.sketch_text.stroke-267"),sQuery(id+"F1.wireOp",EDGE,"E128.sketch_text.stroke-268"),sQuery(id+"F1.wireOp",EDGE,"E128.sketch_text.stroke-269"),sQuery(id+"F1.wireOp",EDGE,"E128.sketch_text.stroke-270"),sQuery(id+"F1.wireOp",EDGE,"E128.sketch_text.stroke-271"),sQuery(id+"F1.wireOp",EDGE,"E128.sketch_text.stroke-272"),sQuery(id+"F1.wireOp",EDGE,"E128.sketch_text.stroke-273"),sQuery(id+"F1.wireOp",EDGE,"E128.sketch_text.stroke-274"),sQuery(id+"F1.wireOp",EDGE,"E128.sketch_text.stroke-275"),sQuery(id+"F1.wireOp",EDGE,"E128.sketch_text.stroke-276"),sQuery(id+"F1.wireOp",EDGE,"E128.sketch_text.stroke-277"),sQuery(id+"F1.wireOp",EDGE,"E128.sketch_text.stroke-278")])]});
            var Q50;
            Q50=makeQuery(id+"F4.opExtrude","SWEPT_BODY",BODY,{"disambiguationData":[OSD([sQuery(id+"F1.wireOp",EDGE,"E128.sketch_text.stroke-279"),sQuery(id+"F1.wireOp",EDGE,"E128.sketch_text.stroke-280"),sQuery(id+"F1.wireOp",EDGE,"E128.sketch_text.stroke-281"),sQuery(id+"F1.wireOp",EDGE,"E128.sketch_text.stroke-282"),sQuery(id+"F1.wireOp",EDGE,"E128.sketch_text.stroke-283"),sQuery(id+"F1.wireOp",EDGE,"E128.sketch_text.stroke-284"),sQuery(id+"F1.wireOp",EDGE,"E128.sketch_text.stroke-285"),sQuery(id+"F1.wireOp",EDGE,"E128.sketch_text.stroke-286"),sQuery(id+"F1.wireOp",EDGE,"E128.sketch_text.stroke-287"),sQuery(id+"F1.wireOp",EDGE,"E128.sketch_text.stroke-288"),sQuery(id+"F1.wireOp",EDGE,"E128.sketch_text.stroke-289"),sQuery(id+"F1.wireOp",EDGE,"E128.sketch_text.stroke-290")])]});
            booleanBodies(context, id + "F5", {"operationType" : BooleanOperationType.UNION, "tools" : qUnion([Q0, Q1, Q2, Q3, Q4, Q5, Q6, Q7, Q8, Q9, Q10, Q11, Q12, Q13, Q14, Q15, Q16, Q17, Q18, Q19, Q20, Q21, Q22, Q23, Q24, Q25, Q26, Q27, Q28, Q29, Q30, Q31, Q32, Q33, Q34, Q35, Q36, Q37, Q38, Q39, Q40, Q41, Q42, Q43, Q44, Q45, Q46, Q47, Q48, Q49, Q50])});
        }
        {
            var Q0;
            Q0=makeQuery(id+"F0.imprint","IMPRINT",FACE,{"disambiguationData":[TD([[makeQuery(id+"F0.imprint","IMPRINT",EDGE,{"derivedFrom":sQuery(id+"F0.wireOp",EDGE,"E6.bottom")}),1.0]])]});
            var Q1;
            Q1=makeQuery(id+"F0.imprint","IMPRINT",FACE,{"disambiguationData":[TD([[makeQuery(id+"F0.imprint","IMPRINT",EDGE,{"derivedFrom":sQuery(id+"F0.wireOp",EDGE,"E0.bottom")}),-1.0]])]});
            extrude(context, id + "F6", {"entities" : qUnion([Q0, Q1]), "operationType" : NewBodyOperationType.REMOVE, "depth" : 3 * mm, "offsetDistance" : 25 * mm});
        }
        {
            var Q0;
            Q0=makeQuery(id+"F0.imprint","IMPRINT",FACE,{"disambiguationData":[TD([[makeQuery(id+"F0.imprint","IMPRINT",EDGE,{"derivedFrom":sQuery(id+"F0.wireOp",EDGE,"E2")}),1.0]])]});
            var Q1;
            Q1=makeQuery(id+"F0.imprint","IMPRINT",FACE,{"disambiguationData":[TD([[makeQuery(id+"F0.imprint","IMPRINT",EDGE,{"derivedFrom":sQuery(id+"F0.wireOp",EDGE,"E1")}),1.0]])]});
            var Q2;
            Q2=makeQuery(id+"F0.imprint","IMPRINT",FACE,{"disambiguationData":[TD([[makeQuery(id+"F0.imprint","IMPRINT",EDGE,{"derivedFrom":sQuery(id+"F0.wireOp",EDGE,"E3")}),1.0]])]});
            var Q3;
            Q3=makeQuery(id+"F0.imprint","IMPRINT",FACE,{"disambiguationData":[TD([[makeQuery(id+"F0.imprint","IMPRINT",EDGE,{"derivedFrom":sQuery(id+"F0.wireOp",EDGE,"E4")}),1.0]])]});
            extrude(context, id + "F7", {"entities" : qUnion([Q0, Q1, Q2, Q3]), "operationType" : NewBodyOperationType.REMOVE, "depth" : 64 * mm, "offsetDistance" : 25 * mm});
        }
        {
            var Q0;
            {var subQ0=sQuery(id+"F1.wireOp",EDGE,"E44");var subQ1=sQuery(id+"F0.wireOp",EDGE,"E5.left");Q0=makeQuery(id+"F5.opBoolean","SPLIT",EDGE,{"disambiguationData":[TD([makeQuery(id+"F2.opExtrude","SWEPT_FACE",FACE,{"disambiguationData":[OSD([subQ0])]})])],"derivedFrom":makeQuery(id+"F2.opExtrude","CAP_EDGE",EDGE,{"disambiguationData":[OSD([subQ1])],"isStart":false})});}
            var Q1;
            {var subQ1=sQuery(id+"F1.wireOp",EDGE,"E44");var subQ2=sQuery(id+"F0.wireOp",EDGE,"E5.left");Q1=makeQuery(id+"F5.opBoolean","SPLIT",EDGE,{"disambiguationData":[TD([makeQuery(id+"F2.opExtrude","SWEPT_FACE",FACE,{"disambiguationData":[OSD([subQ2])]})])],"derivedFrom":makeQuery(id+"F2.opExtrude","CAP_EDGE",EDGE,{"disambiguationData":[OSD([subQ1])],"isStart":false})});}
            var Q2;
            Q2=makeQuery(id+"F2.opExtrude","CAP_EDGE",EDGE,{"disambiguationData":[OSD([sQuery(id+"F1.wireOp",EDGE,"E45")])],"isStart":false});
            var Q3;
            Q3=makeQuery(id+"F5.opBoolean","MERGE",EDGE,{"disambiguationData":[OD(0.0)],"derivedFrom":[makeQuery(id+"F2.opExtrude","CAP_EDGE",EDGE,{"disambiguationData":[OSD([sQuery(id+"F0.wireOp",EDGE,"E5.right")])],"isStart":false}),makeQuery(id+"F2.opExtrude","CAP_EDGE",EDGE,{"disambiguationData":[OSD([sQuery(id+"F1.wireOp",EDGE,"E46"),sQuery(id+"F1.wireOp",EDGE,"E126")])],"isStart":false})]});
            var Q4;
            Q4=makeQuery(id+"F2.opExtrude","CAP_EDGE",EDGE,{"disambiguationData":[OSD([sQuery(id+"F0.wireOp",EDGE,"E6.right")])],"isStart":false});
            var Q5;
            {var subQ0=sQuery(id+"F1.wireOp",EDGE,"E129");var subQ1=sQuery(id+"F1.wireOp",EDGE,"E125");var subQ2=sQuery(id+"F0.wireOp",EDGE,"E8");Q5=makeQuery(id+"F5.opBoolean","SPLIT",EDGE,{"disambiguationData":[TD([makeQuery(id+"F2.opExtrude","SWEPT_FACE",FACE,{"disambiguationData":[OSD([subQ2])]})])],"derivedFrom":makeQuery(id+"F2.opExtrude","CAP_EDGE",EDGE,{"disambiguationData":[OSD([subQ1,subQ0])],"isStart":false})});}
            var Q6;
            {var subQ1=sQuery(id+"F1.wireOp",EDGE,"E129");var subQ2=sQuery(id+"F1.wireOp",EDGE,"E125");var subQ3=sQuery(id+"F0.wireOp",EDGE,"E6.left");Q6=makeQuery(id+"F5.opBoolean","SPLIT",EDGE,{"disambiguationData":[TD([makeQuery(id+"F2.opExtrude","SWEPT_FACE",FACE,{"disambiguationData":[OSD([subQ3])]})])],"derivedFrom":makeQuery(id+"F2.opExtrude","CAP_EDGE",EDGE,{"disambiguationData":[OSD([subQ2,subQ1])],"isStart":false})});}
            var Q7;
            Q7=makeQuery(id+"F2.opExtrude","CAP_EDGE",EDGE,{"disambiguationData":[OSD([sQuery(id+"F0.wireOp",EDGE,"E6.left")])],"isStart":false});
            var Q8;
            {var subQ1=sQuery(id+"F1.wireOp",EDGE,"E44");var subQ2=sQuery(id+"F0.wireOp",EDGE,"E6.right");Q8=makeQuery(id+"F5.opBoolean","SPLIT",EDGE,{"disambiguationData":[TD([makeQuery(id+"F2.opExtrude","SWEPT_FACE",FACE,{"disambiguationData":[OSD([subQ2])]})])],"derivedFrom":makeQuery(id+"F2.opExtrude","CAP_EDGE",EDGE,{"disambiguationData":[OSD([subQ1])],"isStart":false})});}
            var Q9;
            Q9=makeQuery(id+"F2.opExtrude","CAP_EDGE",EDGE,{"disambiguationData":[OSD([sQuery(id+"F1.wireOp",EDGE,"E132")])],"isStart":false});
            var Q10;
            Q10=makeQuery(id+"F2.opExtrude","CAP_EDGE",EDGE,{"disambiguationData":[OSD([sQuery(id+"F0.wireOp",EDGE,"E8")])],"isStart":false});
            var Q11;
            Q11=makeQuery(id+"F2.opExtrude","CAP_EDGE",EDGE,{"disambiguationData":[OSD([sQuery(id+"F0.wireOp",EDGE,"E7")])],"isStart":false});
            fillet(context, id + "F8", {"entities" : qUnion([Q0, Q1, Q2, Q3, Q4, Q5, Q6, Q7, Q8, Q9, Q10, Q11]), "radius" : 2 * mm, "tangentPropagation" : true, "allowEdgeOverflow" : false});
        }
    });
